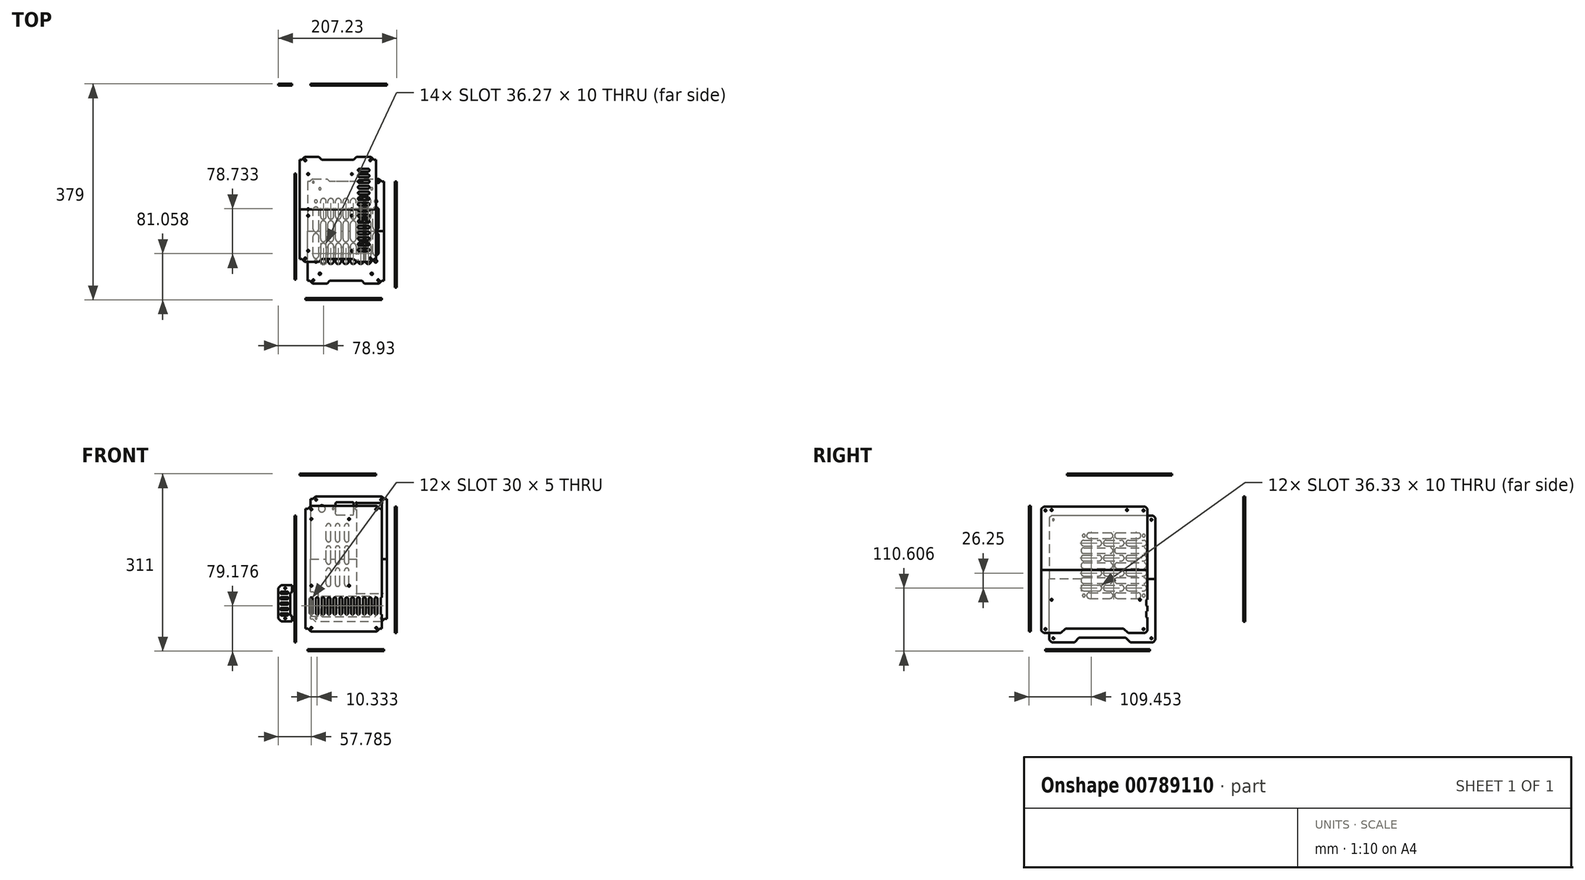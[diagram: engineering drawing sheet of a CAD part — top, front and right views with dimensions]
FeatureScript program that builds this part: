
annotation { "Feature Type Name" : "Feature", "Feature Type Description" : "" }
export const myFeature = defineFeature(function(context is Context, id is Id, definition is map)
    precondition{}
    {
        {
            var Q0;
            Q0=qCreatedBy(makeId("Front.planeOp"),FACE);
            var sketch = newSketch(context, id + "F0", { "sketchPlane" : qUnion([Q0])});
            skLineSegment(sketch, "E0.bottom", {"start": v(-76.44, 105.68) * mm, "end": v(57.56, 105.68) * mm});
            skLineSegment(sketch, "E0.top", {"start": v(-76.44, -8.32) * mm, "end": v(57.56, -8.32) * mm});
            skLineSegment(sketch, "E0.left", {"start": v(-76.44, 105.68) * mm, "end": v(-76.44, -8.32) * mm});
            skLineSegment(sketch, "E0.right", {"start": v(57.56, 105.68) * mm, "end": v(57.56, -8.32) * mm});
            skLineSegment(sketch, "E1", {"start": v(-76.44, 96.68) * mm, "end": v(-72.44, 96.68) * mm});
            skLineSegment(sketch, "E2", {"start": v(-72.44, 96.68) * mm, "end": v(-67.44, 101.68) * mm});
            skLineSegment(sketch, "E3", {"start": v(57.56, 96.68) * mm, "end": v(53.56, 96.68) * mm});
            skLineSegment(sketch, "E4", {"start": v(48.56, 101.68) * mm, "end": v(-67.44, 101.68) * mm});
            skLineSegment(sketch, "E5", {"start": v(48.56, 101.68) * mm, "end": v(53.56, 96.68) * mm});
            skLineSegment(sketch, "E6", {"start": v(-76.44, 95.68) * mm, "end": v(-66.44, 95.68) * mm, "construction": true});
            skCircle(sketch, "E7", {"center": v(-66.44, 95.68) * mm, "radius": 1.6 * mm});
            skLineSegment(sketch, "E8", {"start": v(57.56, 95.68) * mm, "end": v(47.56, 95.68) * mm, "construction": true});
            skCircle(sketch, "E9", {"center": v(47.56, 95.68) * mm, "radius": 1.6 * mm});
            skSolve(sketch);
        }
        {
            var Q0;
            {var subQ1=sQuery(id+"F0.wireOp",EDGE,"E0.top");Q0=makeQuery(id+"F0.imprint","IMPRINT",FACE,{"disambiguationData":[TD([[makeQuery(id+"F0.imprint","IMPRINT",EDGE,{"derivedFrom":subQ1}),1.0]])]});}
            extrude(context, id + "F1", {"entities" : qUnion([Q0]), "depth" : 3 * mm});
        }
        {
            var Q0;
            Q0=makeQuery(id+"F1.opExtrude","SWEPT_BODY",BODY,{"disambiguationData":[OSD([sQuery(id+"F0.wireOp",EDGE,"E0.bottom"),sQuery(id+"F0.wireOp",EDGE,"E0.top"),sQuery(id+"F0.wireOp",EDGE,"E0.left"),sQuery(id+"F0.wireOp",EDGE,"E0.right"),sQuery(id+"F0.wireOp",EDGE,"E1"),sQuery(id+"F0.wireOp",EDGE,"E2"),sQuery(id+"F0.wireOp",EDGE,"8kIEKiAh-QTEb-dtpp-JcTS-wpPMPQfBbqQd"),sQuery(id+"F0.wireOp",EDGE,"IAD0FTGy-GJaP-wMLm-guci-XfnhwucHu2uu"),sQuery(id+"F0.wireOp",EDGE,"IvHsRxJE-VIxi-RXbs-pRJC-tqeUj7lQNFDg"),sQuery(id+"F0.wireOp",EDGE,"jDx6nEBO-jJHg-Gf5S-wIms-nsZNRVFYcTxt")])]});
            var Q1;
            Q1=makeQuery(id+"F1.opExtrude","SWEPT_FACE",FACE,{"disambiguationData":[OSD([sQuery(id+"F0.wireOp",EDGE,"E0.top")])]});
            mirror(context, id + "F2", {"operationType" : NewBodyOperationType.ADD, "entities" : qUnion([Q0]), "mirrorPlane" : qUnion([Q1])});
        }
        {
            var Q0;
            {var subQ0=makeQuery(id+"F1.opExtrude","CAP_FACE",FACE,{"disambiguationData":[OSD([sQuery(id+"F0.wireOp",EDGE,"E0.bottom"),sQuery(id+"F0.wireOp",EDGE,"E0.top"),sQuery(id+"F0.wireOp",EDGE,"E0.left"),sQuery(id+"F0.wireOp",EDGE,"E0.right"),sQuery(id+"F0.wireOp",EDGE,"E1"),sQuery(id+"F0.wireOp",EDGE,"E2"),sQuery(id+"F0.wireOp",EDGE,"8kIEKiAh-QTEb-dtpp-JcTS-wpPMPQfBbqQd"),sQuery(id+"F0.wireOp",EDGE,"IAD0FTGy-GJaP-wMLm-guci-XfnhwucHu2uu"),sQuery(id+"F0.wireOp",EDGE,"IvHsRxJE-VIxi-RXbs-pRJC-tqeUj7lQNFDg"),sQuery(id+"F0.wireOp",EDGE,"jDx6nEBO-jJHg-Gf5S-wIms-nsZNRVFYcTxt")])],"isStart":false});Q0=makeQuery(id+"F2.boolean.opBoolean","MERGE",FACE,{"derivedFrom":[subQ0,makeQuery(id+"F2.opPattern","COPY",FACE,{"derivedFrom":subQ0,"instanceName":"1"})]});}
            var sketch = newSketch(context, id + "F3", { "sketchPlane" : qUnion([Q0])});
            skLineSegment(sketch, "E10", {"start": v(-66.44, -86.32) * mm, "end": v(-66.44, -118.32) * mm, "construction": true});
            skLineSegment(sketch, "E11.bottom", {"start": v(-66.44, 78.68) * mm, "end": v(-0.24, 78.68) * mm, "construction": true});
            skLineSegment(sketch, "E11.top", {"start": v(-66.44, -38.32) * mm, "end": v(-0.24, -38.32) * mm, "construction": true});
            skLineSegment(sketch, "E11.left", {"start": v(-66.44, 78.68) * mm, "end": v(-66.44, -38.32) * mm, "construction": true});
            skLineSegment(sketch, "E11.right", {"start": v(-0.24, 78.68) * mm, "end": v(-0.24, -38.32) * mm, "construction": true});
            skLineSegment(sketch, "E12", {"start": v(-66.44, 78.68) * mm, "end": v(-76.44, 78.68) * mm, "construction": true});
            skCircle(sketch, "E13", {"center": v(-0.24, 78.68) * mm, "radius": 1.6 * mm});
            skCircle(sketch, "E14", {"center": v(-66.44, 78.68) * mm, "radius": 1.6 * mm});
            skCircle(sketch, "E15", {"center": v(-66.44, -38.32) * mm, "radius": 1.6 * mm});
            skCircle(sketch, "E16", {"center": v(-0.24, -38.32) * mm, "radius": 1.6 * mm});
            skLineSegment(sketch, "E17", {"start": v(-66.44, -86.32) * mm, "end": v(-66.44, -61.32) * mm, "construction": true});
            skArc(sketch, "E18.0.startCap", {"start": v(-63.94, -86.32) * mm, "mid": v(-66.44, -88.82) * mm, "end": v(-68.94, -86.32) * mm});
            skArc(sketch, "E18.0.endCap", {"start": v(-68.94, -61.32) * mm, "mid": v(-66.44, -58.82) * mm, "end": v(-63.94, -61.32) * mm});
            skLineSegment(sketch, "E18.0.left", {"start": v(-68.94, -86.32) * mm, "end": v(-68.94, -61.32) * mm});
            skLineSegment(sketch, "E18.0.right", {"start": v(-63.94, -86.32) * mm, "end": v(-63.94, -61.32) * mm});
            skLineSegment(sketch, "E19.1.0.0", {"start": v(-56.11, -86.32) * mm, "end": v(-56.11, -61.32) * mm, "construction": true});
            skArc(sketch, "E19.1.0.1", {"start": v(-53.61, -86.32) * mm, "mid": v(-56.11, -88.82) * mm, "end": v(-58.61, -86.32) * mm});
            skArc(sketch, "E19.1.0.2", {"start": v(-58.61, -61.32) * mm, "mid": v(-56.11, -58.82) * mm, "end": v(-53.61, -61.32) * mm});
            skLineSegment(sketch, "E19.1.0.3", {"start": v(-53.61, -86.32) * mm, "end": v(-53.61, -61.32) * mm});
            skLineSegment(sketch, "E19.1.0.4", {"start": v(-58.61, -86.32) * mm, "end": v(-58.61, -61.32) * mm});
            skLineSegment(sketch, "E19.2.0.0", {"start": v(-45.78, -86.32) * mm, "end": v(-45.78, -61.32) * mm, "construction": true});
            skArc(sketch, "E19.2.0.1", {"start": v(-43.28, -86.32) * mm, "mid": v(-45.78, -88.82) * mm, "end": v(-48.28, -86.32) * mm});
            skArc(sketch, "E19.2.0.2", {"start": v(-48.28, -61.32) * mm, "mid": v(-45.78, -58.82) * mm, "end": v(-43.28, -61.32) * mm});
            skLineSegment(sketch, "E19.2.0.3", {"start": v(-43.28, -86.32) * mm, "end": v(-43.28, -61.32) * mm});
            skLineSegment(sketch, "E19.2.0.4", {"start": v(-48.28, -86.32) * mm, "end": v(-48.28, -61.32) * mm});
            skLineSegment(sketch, "E19.3.0.0", {"start": v(-35.45, -86.32) * mm, "end": v(-35.45, -61.32) * mm, "construction": true});
            skArc(sketch, "E19.3.0.1", {"start": v(-32.95, -86.32) * mm, "mid": v(-35.45, -88.82) * mm, "end": v(-37.95, -86.32) * mm});
            skArc(sketch, "E19.3.0.2", {"start": v(-37.95, -61.32) * mm, "mid": v(-35.45, -58.82) * mm, "end": v(-32.95, -61.32) * mm});
            skLineSegment(sketch, "E19.3.0.3", {"start": v(-32.95, -86.32) * mm, "end": v(-32.95, -61.32) * mm});
            skLineSegment(sketch, "E19.3.0.4", {"start": v(-37.95, -86.32) * mm, "end": v(-37.95, -61.32) * mm});
            skLineSegment(sketch, "E19.4.0.0", {"start": v(-25.11, -86.32) * mm, "end": v(-25.11, -61.32) * mm, "construction": true});
            skArc(sketch, "E19.4.0.1", {"start": v(-22.61, -86.32) * mm, "mid": v(-25.11, -88.82) * mm, "end": v(-27.61, -86.32) * mm});
            skArc(sketch, "E19.4.0.2", {"start": v(-27.61, -61.32) * mm, "mid": v(-25.11, -58.82) * mm, "end": v(-22.61, -61.32) * mm});
            skLineSegment(sketch, "E19.4.0.3", {"start": v(-22.61, -86.32) * mm, "end": v(-22.61, -61.32) * mm});
            skLineSegment(sketch, "E19.4.0.4", {"start": v(-27.61, -86.32) * mm, "end": v(-27.61, -61.32) * mm});
            skLineSegment(sketch, "E19.5.0.0", {"start": v(-14.78, -86.32) * mm, "end": v(-14.78, -61.32) * mm, "construction": true});
            skArc(sketch, "E19.5.0.1", {"start": v(-12.28, -86.32) * mm, "mid": v(-14.78, -88.82) * mm, "end": v(-17.28, -86.32) * mm});
            skArc(sketch, "E19.5.0.2", {"start": v(-17.28, -61.32) * mm, "mid": v(-14.78, -58.82) * mm, "end": v(-12.28, -61.32) * mm});
            skLineSegment(sketch, "E19.5.0.3", {"start": v(-12.28, -86.32) * mm, "end": v(-12.28, -61.32) * mm});
            skLineSegment(sketch, "E19.5.0.4", {"start": v(-17.28, -86.32) * mm, "end": v(-17.28, -61.32) * mm});
            skLineSegment(sketch, "E19.6.0.0", {"start": v(-4.45, -86.32) * mm, "end": v(-4.45, -61.32) * mm, "construction": true});
            skArc(sketch, "E19.6.0.1", {"start": v(-1.95, -86.32) * mm, "mid": v(-4.45, -88.82) * mm, "end": v(-6.95, -86.32) * mm});
            skArc(sketch, "E19.6.0.2", {"start": v(-6.95, -61.32) * mm, "mid": v(-4.45, -58.82) * mm, "end": v(-1.95, -61.32) * mm});
            skLineSegment(sketch, "E19.6.0.3", {"start": v(-1.95, -86.32) * mm, "end": v(-1.95, -61.32) * mm});
            skLineSegment(sketch, "E19.6.0.4", {"start": v(-6.95, -86.32) * mm, "end": v(-6.95, -61.32) * mm});
            skLineSegment(sketch, "E19.7.0.0", {"start": v(5.89, -86.32) * mm, "end": v(5.89, -61.32) * mm, "construction": true});
            skArc(sketch, "E19.7.0.1", {"start": v(8.39, -86.32) * mm, "mid": v(5.89, -88.82) * mm, "end": v(3.39, -86.32) * mm});
            skArc(sketch, "E19.7.0.2", {"start": v(3.39, -61.32) * mm, "mid": v(5.89, -58.82) * mm, "end": v(8.39, -61.32) * mm});
            skLineSegment(sketch, "E19.7.0.3", {"start": v(8.39, -86.32) * mm, "end": v(8.39, -61.32) * mm});
            skLineSegment(sketch, "E19.7.0.4", {"start": v(3.39, -86.32) * mm, "end": v(3.39, -61.32) * mm});
            skLineSegment(sketch, "E19.8.0.0", {"start": v(16.22, -86.32) * mm, "end": v(16.22, -61.32) * mm, "construction": true});
            skArc(sketch, "E19.8.0.1", {"start": v(18.72, -86.32) * mm, "mid": v(16.22, -88.82) * mm, "end": v(13.72, -86.32) * mm});
            skArc(sketch, "E19.8.0.2", {"start": v(13.72, -61.32) * mm, "mid": v(16.22, -58.82) * mm, "end": v(18.72, -61.32) * mm});
            skLineSegment(sketch, "E19.8.0.3", {"start": v(18.72, -86.32) * mm, "end": v(18.72, -61.32) * mm});
            skLineSegment(sketch, "E19.8.0.4", {"start": v(13.72, -86.32) * mm, "end": v(13.72, -61.32) * mm});
            skLineSegment(sketch, "E19.9.0.0", {"start": v(26.55, -86.32) * mm, "end": v(26.55, -61.32) * mm, "construction": true});
            skArc(sketch, "E19.9.0.1", {"start": v(29.05, -86.32) * mm, "mid": v(26.55, -88.82) * mm, "end": v(24.05, -86.32) * mm});
            skArc(sketch, "E19.9.0.2", {"start": v(24.05, -61.32) * mm, "mid": v(26.55, -58.82) * mm, "end": v(29.05, -61.32) * mm});
            skLineSegment(sketch, "E19.9.0.3", {"start": v(29.05, -86.32) * mm, "end": v(29.05, -61.32) * mm});
            skLineSegment(sketch, "E19.9.0.4", {"start": v(24.05, -86.32) * mm, "end": v(24.05, -61.32) * mm});
            skLineSegment(sketch, "E19.10.0.0", {"start": v(36.89, -86.32) * mm, "end": v(36.89, -61.32) * mm, "construction": true});
            skArc(sketch, "E19.10.0.1", {"start": v(39.39, -86.32) * mm, "mid": v(36.89, -88.82) * mm, "end": v(34.39, -86.32) * mm});
            skArc(sketch, "E19.10.0.2", {"start": v(34.39, -61.32) * mm, "mid": v(36.89, -58.82) * mm, "end": v(39.39, -61.32) * mm});
            skLineSegment(sketch, "E19.10.0.3", {"start": v(39.39, -86.32) * mm, "end": v(39.39, -61.32) * mm});
            skLineSegment(sketch, "E19.10.0.4", {"start": v(34.39, -86.32) * mm, "end": v(34.39, -61.32) * mm});
            skLineSegment(sketch, "E19.11.0.0", {"start": v(47.22, -86.32) * mm, "end": v(47.22, -61.32) * mm, "construction": true});
            skArc(sketch, "E19.11.0.1", {"start": v(49.72, -86.32) * mm, "mid": v(47.22, -88.82) * mm, "end": v(44.72, -86.32) * mm});
            skArc(sketch, "E19.11.0.2", {"start": v(44.72, -61.32) * mm, "mid": v(47.22, -58.82) * mm, "end": v(49.72, -61.32) * mm});
            skLineSegment(sketch, "E19.11.0.3", {"start": v(49.72, -86.32) * mm, "end": v(49.72, -61.32) * mm});
            skLineSegment(sketch, "E19.11.0.4", {"start": v(44.72, -86.32) * mm, "end": v(44.72, -61.32) * mm});
            skLineSegment(sketch, "E19.12.0.0", {"start": v(57.55, -86.32) * mm, "end": v(57.55, -61.32) * mm, "construction": true});
            skArc(sketch, "E19.12.0.1", {"start": v(60.05, -86.32) * mm, "mid": v(57.55, -88.82) * mm, "end": v(55.05, -86.32) * mm});
            skArc(sketch, "E19.12.0.2", {"start": v(55.05, -61.32) * mm, "mid": v(57.55, -58.82) * mm, "end": v(60.05, -61.32) * mm});
            skLineSegment(sketch, "E19.12.0.3", {"start": v(60.05, -86.32) * mm, "end": v(60.05, -61.32) * mm});
            skLineSegment(sketch, "E19.12.0.4", {"start": v(55.05, -86.32) * mm, "end": v(55.05, -61.32) * mm});
            skLineSegment(sketch, "E19.direction1", {"start": v(-68.94, -86.32) * mm, "end": v(-58.61, -86.32) * mm, "construction": true});
            skSolve(sketch);
        }
        {
            var Q0;
            Q0=qSketchRegion(id+"F3",true);
            extrude(context, id + "F4", {"entities" : qUnion([Q0]), "operationType" : NewBodyOperationType.REMOVE, "oppositeDirection" : true, "depth" : 3 * mm});
        }
        {
            var Q0;
            Q0=qCreatedBy(makeId("Right.planeOp"),FACE);
            cPlane(context, id + "F5", {"entities" : qUnion([Q0]), "cplaneType" : CPlaneType.OFFSET, "offset" : 80 * mm, "width" : 150 * mm, "height" : 150 * mm});
        }
        {
            var Q0;
            Q0=qCreatedBy(id+"F5.planeOp",FACE);
            var sketch = newSketch(context, id + "F6", { "sketchPlane" : qUnion([Q0])});
            skLineSegment(sketch, "E20.bottom", {"start": v(18.91, 100.63) * mm, "end": v(204.91, 100.63) * mm});
            skLineSegment(sketch, "E20.top", {"start": v(18.91, -10.37) * mm, "end": v(204.91, -10.37) * mm});
            skLineSegment(sketch, "E20.left", {"start": v(18.91, 100.63) * mm, "end": v(18.91, -10.37) * mm});
            skLineSegment(sketch, "E20.right", {"start": v(204.91, 100.63) * mm, "end": v(204.91, -10.37) * mm});
            skLineSegment(sketch, "E21", {"start": v(18.91, 96.63) * mm, "end": v(22.91, 100.63) * mm});
            skLineSegment(sketch, "E22", {"start": v(200.91, 100.63) * mm, "end": v(204.91, 96.63) * mm});
            skLineSegment(sketch, "E23", {"start": v(18.91, 93.63) * mm, "end": v(25.91, 93.63) * mm, "construction": true});
            skCircle(sketch, "E24", {"center": v(25.91, 93.63) * mm, "radius": 1.6 * mm});
            skLineSegment(sketch, "E25", {"start": v(204.91, 93.63) * mm, "end": v(197.91, 93.63) * mm, "construction": true});
            skCircle(sketch, "E26", {"center": v(197.91, 93.63) * mm, "radius": 1.6 * mm});
            skSolve(sketch);
        }
        {
            var Q0;
            {var subQ4=sQuery(id+"F6.wireOp",EDGE,"E20.top");Q0=makeQuery(id+"F6.imprint","IMPRINT",FACE,{"disambiguationData":[TD([[makeQuery(id+"F6.imprint","IMPRINT",EDGE,{"derivedFrom":subQ4}),1.0]])]});}
            extrude(context, id + "F7", {"entities" : qUnion([Q0]), "depth" : 3 * mm});
        }
        {
            var Q0;
            Q0=makeQuery(id+"F7.opExtrude","SWEPT_BODY",BODY,{"disambiguationData":[OSD([sQuery(id+"F6.wireOp",EDGE,"E20.bottom"),sQuery(id+"F6.wireOp",EDGE,"E20.top"),sQuery(id+"F6.wireOp",EDGE,"E20.left"),sQuery(id+"F6.wireOp",EDGE,"E20.right"),sQuery(id+"F6.wireOp",EDGE,"uhohLnhp-hqEh-HnCf-sw5P-UAyFwgDYjcBT"),sQuery(id+"F6.wireOp",EDGE,"PZ9vbapj-Vyhe-IVd5-wSIB-ihSb0FTefDFo"),sQuery(id+"F6.wireOp",EDGE,"Vy2RlQAS-aQ6k-OJzX-lqoE-WAFZ4NoHzz8E"),sQuery(id+"F6.wireOp",EDGE,"uOpGianr-bHoC-LPpd-ZrnQ-WT6fRq75YZDk"),sQuery(id+"F6.wireOp",EDGE,"ByD4MoDk-9vtG-w2Bj-nV2I-deXss6nWGu8L"),sQuery(id+"F6.wireOp",EDGE,"dErzSW6J-HGX5-GNXE-lozc-OmhnMsFbACEc"),sQuery(id+"F6.wireOp",EDGE,"oiYVu7ST-duG0-g5FE-uATR-zlAqLM0uh895"),sQuery(id+"F6.wireOp",EDGE,"fhnCciFL-T4Vn-rBCZ-nkKt-uSig2OXv9zq8")])]});
            var Q1;
            Q1=makeQuery(id+"F7.opExtrude","SWEPT_FACE",FACE,{"disambiguationData":[OSD([sQuery(id+"F6.wireOp",EDGE,"E20.top")])]});
            mirror(context, id + "F8", {"operationType" : NewBodyOperationType.ADD, "entities" : qUnion([Q0]), "mirrorPlane" : qUnion([Q1])});
        }
        {
            var Q0;
            {var subQ0=makeQuery(id+"F7.opExtrude","CAP_FACE",FACE,{"disambiguationData":[OSD([sQuery(id+"F6.wireOp",EDGE,"E20.bottom"),sQuery(id+"F6.wireOp",EDGE,"E20.top"),sQuery(id+"F6.wireOp",EDGE,"E20.left"),sQuery(id+"F6.wireOp",EDGE,"E20.right"),sQuery(id+"F6.wireOp",EDGE,"E21"),sQuery(id+"F6.wireOp",EDGE,"E22")])],"isStart":true});Q0=makeQuery(id+"F8.boolean.opBoolean","MERGE",FACE,{"derivedFrom":[subQ0,makeQuery(id+"F8.opPattern","COPY",FACE,{"derivedFrom":subQ0,"instanceName":"1"})]});}
            var sketch = newSketch(context, id + "F9", { "sketchPlane" : qUnion([Q0])});
            skLineSegment(sketch, "E27", {"start": v(-201.91, -69.37) * mm, "end": v(-201.91, 100.63) * mm, "construction": true});
            skLineSegment(sketch, "E28", {"start": v(-201.91, -69.37) * mm, "end": v(-31.91, -69.37) * mm, "construction": true});
            skLineSegment(sketch, "E29", {"start": v(-201.91, 100.63) * mm, "end": v(-31.91, 100.63) * mm, "construction": true});
            skLineSegment(sketch, "E30", {"start": v(-31.91, 100.63) * mm, "end": v(-31.91, -69.37) * mm, "construction": true});
            skLineSegment(sketch, "E31", {"start": v(-201.91, -62.97) * mm, "end": v(-191.71, -62.97) * mm, "construction": true});
            skCircle(sketch, "E32", {"center": v(-191.71, -62.97) * mm, "radius": 1.5 * mm});
            skLineSegment(sketch, "E33", {"start": v(-191.71, -62.97) * mm, "end": v(-36.81, -62.97) * mm, "construction": true});
            skCircle(sketch, "E34", {"center": v(-36.81, -62.97) * mm, "radius": 1.5 * mm});
            skLineSegment(sketch, "E35", {"start": v(-201.91, 94.43) * mm, "end": v(-168.91, 94.43) * mm, "construction": true});
            skCircle(sketch, "E36", {"center": v(-168.91, 94.43) * mm, "radius": 1.5 * mm});
            skLineSegment(sketch, "E37", {"start": v(-168.91, 94.43) * mm, "end": v(-36.81, 94.43) * mm, "construction": true});
            skCircle(sketch, "E38", {"center": v(-36.81, 94.43) * mm, "radius": 1.5 * mm});
            skLineSegment(sketch, "E39", {"start": v(-52.91, -121.37) * mm, "end": v(-60.91, -113.37) * mm});
            skLineSegment(sketch, "E40", {"start": v(-60.91, -113.37) * mm, "end": v(-162.91, -113.37) * mm});
            skLineSegment(sketch, "E41", {"start": v(-162.91, -113.37) * mm, "end": v(-170.91, -121.37) * mm});
            skLineSegment(sketch, "E42", {"start": v(-52.91, -121.37) * mm, "end": v(-170.91, -121.37) * mm});
            skLineSegment(sketch, "E43.bottom", {"start": v(-202.91, -62.57) * mm, "end": v(-204.91, -62.57) * mm});
            skLineSegment(sketch, "E43.top", {"start": v(-202.91, -73.57) * mm, "end": v(-204.91, -73.57) * mm});
            skLineSegment(sketch, "E43.left", {"start": v(-202.91, -62.57) * mm, "end": v(-202.91, -73.57) * mm});
            skLineSegment(sketch, "E43.right", {"start": v(-204.91, -62.57) * mm, "end": v(-204.91, -73.57) * mm});
            skLineSegment(sketch, "E44", {"start": v(-202.91, -68.07) * mm, "end": v(-201.91, -68.07) * mm, "construction": true});
            skLineSegment(sketch, "E45.bottom", {"start": v(-202.91, -82.87) * mm, "end": v(-204.91, -82.87) * mm});
            skLineSegment(sketch, "E45.top", {"start": v(-202.91, -93.87) * mm, "end": v(-204.91, -93.87) * mm});
            skLineSegment(sketch, "E45.left", {"start": v(-202.91, -82.87) * mm, "end": v(-202.91, -93.87) * mm});
            skLineSegment(sketch, "E45.right", {"start": v(-204.91, -82.87) * mm, "end": v(-204.91, -93.87) * mm});
            skLineSegment(sketch, "E46", {"start": v(-204.91, -82.87) * mm, "end": v(-204.91, -73.57) * mm, "construction": true});
            skLineSegment(sketch, "E47", {"start": v(-202.91, -73.57) * mm, "end": v(-202.91, -82.87) * mm, "construction": true});
            skLineSegment(sketch, "E48", {"start": v(-204.91, -88.37) * mm, "end": v(-207.88, -88.37) * mm, "construction": true});
            skLineSegment(sketch, "E49", {"start": v(-207.88, -88.37) * mm, "end": v(-207.88, -68.07) * mm, "construction": true});
            skPoint(sketch, "E49.endSnap0", {"position": v(-204.91, -68.07) * mm});
            skLineSegment(sketch, "E50", {"start": v(-207.88, -68.07) * mm, "end": v(-204.91, -68.07) * mm, "construction": true});
            skSolve(sketch);
        }
        {
            var Q0;
            Q0=qSketchRegion(id+"F9",true);
            var Q1;
            {var subQ0=sQuery(id+"F9.wireOp",EDGE,"b6TVsvgF-kPWZ-6Ni7-LZi2-MRGtpnM4VBQ9");Q1=makeQuery(id+"F9.imprint","IMPRINT",FACE,{"disambiguationData":[TD([[makeQuery(id+"F9.imprint","IMPRINT",EDGE,{"derivedFrom":subQ0}),-1.0]])]});}
            extrude(context, id + "F10", {"entities" : qUnion([Q0, Q1]), "operationType" : NewBodyOperationType.REMOVE, "oppositeDirection" : true, "depth" : 25 * mm});
        }
        {
            var Q0;
            Q0=qCreatedBy(makeId("Right.planeOp"),FACE);
            cPlane(context, id + "F11", {"entities" : qUnion([Q0]), "cplaneType" : CPlaneType.OFFSET, "offset" : 96 * mm, "oppositeDirection" : true, "width" : 150 * mm, "height" : 150 * mm});
        }
        {
            var Q0;
            Q0=qCreatedBy(id+"F11.planeOp",FACE);
            var sketch = newSketch(context, id + "F12", { "sketchPlane" : qUnion([Q0])});
            skLineSegment(sketch, "E51.bottom", {"start": v(218.79, 84.48) * mm, "end": v(32.79, 84.48) * mm});
            skLineSegment(sketch, "E51.top", {"start": v(218.79, -26.52) * mm, "end": v(32.79, -26.52) * mm});
            skLineSegment(sketch, "E51.left", {"start": v(218.79, 84.48) * mm, "end": v(218.79, -26.52) * mm});
            skLineSegment(sketch, "E51.right", {"start": v(32.79, 84.48) * mm, "end": v(32.79, -26.52) * mm});
            skLineSegment(sketch, "E52", {"start": v(218.79, 80.48) * mm, "end": v(214.79, 84.48) * mm});
            skLineSegment(sketch, "E53", {"start": v(36.79, 84.48) * mm, "end": v(32.79, 80.48) * mm});
            skLineSegment(sketch, "E54", {"start": v(218.79, 77.48) * mm, "end": v(211.79, 77.48) * mm, "construction": true});
            skCircle(sketch, "E55", {"center": v(211.79, 77.48) * mm, "radius": 1.6 * mm});
            skLineSegment(sketch, "E56", {"start": v(32.79, 77.48) * mm, "end": v(39.79, 77.48) * mm, "construction": true});
            skCircle(sketch, "E57", {"center": v(39.79, 77.48) * mm, "radius": 1.6 * mm});
            skSolve(sketch);
        }
        {
            var Q0;
            {var subQ1=sQuery(id+"F12.wireOp",EDGE,"E51.top");Q0=makeQuery(id+"F12.imprint","IMPRINT",FACE,{"disambiguationData":[TD([[makeQuery(id+"F12.imprint","IMPRINT",EDGE,{"derivedFrom":subQ1}),-1.0]])]});}
            extrude(context, id + "F13", {"entities" : qUnion([Q0]), "depth" : 3 * mm});
        }
        {
            var Q0;
            Q0=makeQuery(id+"F13.opExtrude","SWEPT_BODY",BODY,{"disambiguationData":[OSD([sQuery(id+"F12.wireOp",EDGE,"E51.bottom"),sQuery(id+"F12.wireOp",EDGE,"E51.top"),sQuery(id+"F12.wireOp",EDGE,"E51.left"),sQuery(id+"F12.wireOp",EDGE,"E51.right"),sQuery(id+"F12.wireOp",EDGE,"E52"),sQuery(id+"F12.wireOp",EDGE,"E53")])]});
            var Q1;
            Q1=makeQuery(id+"F13.opExtrude","SWEPT_FACE",FACE,{"disambiguationData":[OSD([sQuery(id+"F12.wireOp",EDGE,"E51.top")])]});
            mirror(context, id + "F14", {"operationType" : NewBodyOperationType.ADD, "entities" : qUnion([Q0]), "mirrorPlane" : qUnion([Q1])});
        }
        {
            var Q0;
            {var subQ0=makeQuery(id+"F13.opExtrude","CAP_FACE",FACE,{"disambiguationData":[OSD([sQuery(id+"F12.wireOp",EDGE,"E51.bottom"),sQuery(id+"F12.wireOp",EDGE,"E51.top"),sQuery(id+"F12.wireOp",EDGE,"E51.left"),sQuery(id+"F12.wireOp",EDGE,"E51.right"),sQuery(id+"F12.wireOp",EDGE,"E52"),sQuery(id+"F12.wireOp",EDGE,"E53")])],"isStart":true});Q0=makeQuery(id+"F14.boolean.opBoolean","MERGE",FACE,{"derivedFrom":[subQ0,makeQuery(id+"F14.opPattern","COPY",FACE,{"derivedFrom":subQ0,"instanceName":"1"})]});}
            var sketch = newSketch(context, id + "F15", { "sketchPlane" : qUnion([Q0])});
            skLineSegment(sketch, "E58", {"start": v(-218.79, 54.48) * mm, "end": v(-198.29, 54.48) * mm, "construction": true});
            skLineSegment(sketch, "E59", {"start": v(-198.29, 54.48) * mm, "end": v(-198.29, -60.52) * mm, "construction": true});
            skLineSegment(sketch, "E60", {"start": v(-198.29, 49.48) * mm, "end": v(-188.29, 49.48) * mm, "construction": true});
            skLineSegment(sketch, "E61", {"start": v(-188.29, 49.48) * mm, "end": v(-152.29, 49.48) * mm, "construction": true});
            skLineSegment(sketch, "E62", {"start": v(-198.29, 36.36) * mm, "end": v(-171.95, 36.36) * mm, "construction": true});
            skLineSegment(sketch, "E63", {"start": v(-198.29, 23.23) * mm, "end": v(-152.29, 23.23) * mm, "construction": true});
            skLineSegment(sketch, "E64", {"start": v(-198.29, 10.1) * mm, "end": v(-171.95, 10.1) * mm, "construction": true});
            skLineSegment(sketch, "E65", {"start": v(-198.29, -3.02) * mm, "end": v(-152.29, -3.02) * mm, "construction": true});
            skLineSegment(sketch, "E66", {"start": v(-198.29, -16.14) * mm, "end": v(-171.95, -16.14) * mm, "construction": true});
            skLineSegment(sketch, "E67", {"start": v(-198.29, -29.27) * mm, "end": v(-152.29, -29.27) * mm, "construction": true});
            skLineSegment(sketch, "E68", {"start": v(-198.29, -42.4) * mm, "end": v(-171.95, -42.4) * mm, "construction": true});
            skLineSegment(sketch, "E69", {"start": v(-198.29, -55.52) * mm, "end": v(-188.29, -55.52) * mm, "construction": true});
            skLineSegment(sketch, "E70", {"start": v(-188.29, -55.52) * mm, "end": v(-152.29, -55.52) * mm, "construction": true});
            skCircle(sketch, "E71", {"center": v(-198.29, 49.48) * mm, "radius": 2.55 * mm});
            skLineSegment(sketch, "E72", {"start": v(-103.29, 49.48) * mm, "end": v(-93.29, 49.48) * mm, "construction": true});
            skPoint(sketch, "E72.endSnap0", {"position": v(-82.69, 49.48) * mm});
            skCircle(sketch, "E73", {"center": v(-93.29, 49.48) * mm, "radius": 2.55 * mm});
            skLineSegment(sketch, "E74", {"start": v(-152.29, 49.48) * mm, "end": v(-139.29, 49.48) * mm, "construction": true});
            skLineSegment(sketch, "E75", {"start": v(-139.29, 49.48) * mm, "end": v(-103.29, 49.48) * mm, "construction": true});
            skArc(sketch, "E76.0.startCap", {"start": v(-188.29, 44.48) * mm, "mid": v(-193.29, 49.48) * mm, "end": v(-188.29, 54.48) * mm});
            skArc(sketch, "E76.0.endCap", {"start": v(-152.29, 54.48) * mm, "mid": v(-147.29, 49.48) * mm, "end": v(-152.29, 44.48) * mm});
            skLineSegment(sketch, "E76.0.left", {"start": v(-188.29, 54.48) * mm, "end": v(-152.29, 54.48) * mm});
            skLineSegment(sketch, "E76.0.right", {"start": v(-188.29, 44.48) * mm, "end": v(-152.29, 44.48) * mm});
            skArc(sketch, "E76.1.startCap", {"start": v(-139.29, 44.48) * mm, "mid": v(-144.29, 49.48) * mm, "end": v(-139.29, 54.48) * mm});
            skArc(sketch, "E76.1.endCap", {"start": v(-103.29, 54.48) * mm, "mid": v(-98.29, 49.48) * mm, "end": v(-103.29, 44.48) * mm});
            skLineSegment(sketch, "E76.1.left", {"start": v(-139.29, 54.48) * mm, "end": v(-103.29, 54.48) * mm});
            skLineSegment(sketch, "E76.1.right", {"start": v(-139.29, 44.48) * mm, "end": v(-103.29, 44.48) * mm});
            skLineSegment(sketch, "E77", {"start": v(-171.95, 36.36) * mm, "end": v(-158.95, 36.36) * mm, "construction": true});
            skLineSegment(sketch, "E78", {"start": v(-158.95, 36.36) * mm, "end": v(-132.62, 36.36) * mm, "construction": true});
            skLineSegment(sketch, "E79", {"start": v(-132.62, 36.36) * mm, "end": v(-119.62, 36.36) * mm, "construction": true});
            skLineSegment(sketch, "E80", {"start": v(-119.62, 36.36) * mm, "end": v(-93.29, 36.36) * mm, "construction": true});
            skArc(sketch, "E81.0.startCap", {"start": v(-198.29, 31.36) * mm, "mid": v(-203.29, 36.36) * mm, "end": v(-198.29, 41.36) * mm});
            skArc(sketch, "E81.0.endCap", {"start": v(-171.95, 41.36) * mm, "mid": v(-166.95, 36.36) * mm, "end": v(-171.95, 31.36) * mm});
            skLineSegment(sketch, "E81.0.left", {"start": v(-198.29, 41.36) * mm, "end": v(-171.95, 41.36) * mm});
            skLineSegment(sketch, "E81.0.right", {"start": v(-198.29, 31.36) * mm, "end": v(-171.95, 31.36) * mm});
            skArc(sketch, "E81.1.startCap", {"start": v(-158.95, 31.36) * mm, "mid": v(-163.95, 36.36) * mm, "end": v(-158.95, 41.36) * mm});
            skArc(sketch, "E81.1.endCap", {"start": v(-132.62, 41.36) * mm, "mid": v(-127.62, 36.36) * mm, "end": v(-132.62, 31.36) * mm});
            skLineSegment(sketch, "E81.1.left", {"start": v(-158.95, 41.36) * mm, "end": v(-132.62, 41.36) * mm});
            skLineSegment(sketch, "E81.1.right", {"start": v(-158.95, 31.36) * mm, "end": v(-132.62, 31.36) * mm});
            skArc(sketch, "E81.2.startCap", {"start": v(-119.62, 31.36) * mm, "mid": v(-124.62, 36.36) * mm, "end": v(-119.62, 41.36) * mm});
            skArc(sketch, "E81.2.endCap", {"start": v(-93.29, 41.36) * mm, "mid": v(-88.29, 36.36) * mm, "end": v(-93.29, 31.36) * mm});
            skLineSegment(sketch, "E81.2.left", {"start": v(-119.62, 41.36) * mm, "end": v(-93.29, 41.36) * mm});
            skLineSegment(sketch, "E81.2.right", {"start": v(-119.62, 31.36) * mm, "end": v(-93.29, 31.36) * mm});
            skLineSegment(sketch, "E82", {"start": v(-152.29, 23.23) * mm, "end": v(-139.29, 23.23) * mm, "construction": true});
            skLineSegment(sketch, "E83", {"start": v(-139.29, 23.23) * mm, "end": v(-93.29, 23.23) * mm, "construction": true});
            skArc(sketch, "E84.0.startCap", {"start": v(-198.29, 18.23) * mm, "mid": v(-203.29, 23.23) * mm, "end": v(-198.29, 28.23) * mm});
            skArc(sketch, "E84.0.endCap", {"start": v(-152.29, 28.23) * mm, "mid": v(-147.29, 23.23) * mm, "end": v(-152.29, 18.23) * mm});
            skLineSegment(sketch, "E84.0.left", {"start": v(-198.29, 28.23) * mm, "end": v(-152.29, 28.23) * mm});
            skLineSegment(sketch, "E84.0.right", {"start": v(-198.29, 18.23) * mm, "end": v(-152.29, 18.23) * mm});
            skArc(sketch, "E84.1.startCap", {"start": v(-139.29, 18.23) * mm, "mid": v(-144.29, 23.23) * mm, "end": v(-139.29, 28.23) * mm});
            skArc(sketch, "E84.1.endCap", {"start": v(-93.29, 28.23) * mm, "mid": v(-88.29, 23.23) * mm, "end": v(-93.29, 18.23) * mm});
            skLineSegment(sketch, "E84.1.left", {"start": v(-139.29, 28.23) * mm, "end": v(-93.29, 28.23) * mm});
            skLineSegment(sketch, "E84.1.right", {"start": v(-139.29, 18.23) * mm, "end": v(-93.29, 18.23) * mm});
            skLineSegment(sketch, "E85", {"start": v(-171.95, 10.1) * mm, "end": v(-158.95, 10.1) * mm, "construction": true});
            skLineSegment(sketch, "E86", {"start": v(-158.95, 10.1) * mm, "end": v(-132.62, 10.1) * mm, "construction": true});
            skLineSegment(sketch, "E87", {"start": v(-132.62, 10.1) * mm, "end": v(-119.62, 10.1) * mm, "construction": true});
            skLineSegment(sketch, "E88", {"start": v(-119.62, 10.1) * mm, "end": v(-93.29, 10.1) * mm, "construction": true});
            skArc(sketch, "E89.0.startCap", {"start": v(-198.29, 5.1) * mm, "mid": v(-203.29, 10.1) * mm, "end": v(-198.29, 15.1) * mm});
            skArc(sketch, "E89.0.endCap", {"start": v(-171.95, 15.1) * mm, "mid": v(-166.95, 10.1) * mm, "end": v(-171.95, 5.1) * mm});
            skLineSegment(sketch, "E89.0.left", {"start": v(-198.29, 15.1) * mm, "end": v(-171.95, 15.1) * mm});
            skLineSegment(sketch, "E89.0.right", {"start": v(-198.29, 5.1) * mm, "end": v(-171.95, 5.1) * mm});
            skArc(sketch, "E89.1.startCap", {"start": v(-158.95, 5.1) * mm, "mid": v(-163.95, 10.1) * mm, "end": v(-158.95, 15.1) * mm});
            skArc(sketch, "E89.1.endCap", {"start": v(-132.62, 15.1) * mm, "mid": v(-127.62, 10.1) * mm, "end": v(-132.62, 5.1) * mm});
            skLineSegment(sketch, "E89.1.left", {"start": v(-158.95, 15.1) * mm, "end": v(-132.62, 15.1) * mm});
            skLineSegment(sketch, "E89.1.right", {"start": v(-158.95, 5.1) * mm, "end": v(-132.62, 5.1) * mm});
            skArc(sketch, "E89.2.startCap", {"start": v(-119.62, 5.1) * mm, "mid": v(-124.62, 10.1) * mm, "end": v(-119.62, 15.1) * mm});
            skArc(sketch, "E89.2.endCap", {"start": v(-93.29, 15.1) * mm, "mid": v(-88.29, 10.1) * mm, "end": v(-93.29, 5.1) * mm});
            skLineSegment(sketch, "E89.2.left", {"start": v(-119.62, 15.1) * mm, "end": v(-93.29, 15.1) * mm});
            skLineSegment(sketch, "E89.2.right", {"start": v(-119.62, 5.1) * mm, "end": v(-93.29, 5.1) * mm});
            skLineSegment(sketch, "E90", {"start": v(-152.29, -3.02) * mm, "end": v(-139.29, -3.02) * mm, "construction": true});
            skLineSegment(sketch, "E91", {"start": v(-139.29, -3.02) * mm, "end": v(-93.29, -3.02) * mm, "construction": true});
            skLineSegment(sketch, "E92", {"start": v(-171.95, -16.14) * mm, "end": v(-158.95, -16.14) * mm, "construction": true});
            skLineSegment(sketch, "E93", {"start": v(-158.95, -16.14) * mm, "end": v(-132.62, -16.14) * mm, "construction": true});
            skLineSegment(sketch, "E94", {"start": v(-132.62, -16.14) * mm, "end": v(-119.62, -16.14) * mm, "construction": true});
            skLineSegment(sketch, "E95", {"start": v(-119.62, -16.14) * mm, "end": v(-93.29, -16.14) * mm, "construction": true});
            skLineSegment(sketch, "E96", {"start": v(-152.29, -29.27) * mm, "end": v(-139.29, -29.27) * mm, "construction": true});
            skLineSegment(sketch, "E97", {"start": v(-139.29, -29.27) * mm, "end": v(-93.29, -29.27) * mm, "construction": true});
            skLineSegment(sketch, "E98", {"start": v(-171.95, -42.4) * mm, "end": v(-158.95, -42.4) * mm, "construction": true});
            skLineSegment(sketch, "E99", {"start": v(-158.95, -42.4) * mm, "end": v(-132.62, -42.4) * mm, "construction": true});
            skLineSegment(sketch, "E100", {"start": v(-132.62, -42.4) * mm, "end": v(-119.62, -42.4) * mm, "construction": true});
            skLineSegment(sketch, "E101", {"start": v(-119.62, -42.4) * mm, "end": v(-93.29, -42.4) * mm, "construction": true});
            skLineSegment(sketch, "E102", {"start": v(-152.29, -55.52) * mm, "end": v(-139.29, -55.52) * mm, "construction": true});
            skLineSegment(sketch, "E103", {"start": v(-139.29, -55.52) * mm, "end": v(-103.29, -55.52) * mm, "construction": true});
            skLineSegment(sketch, "E104", {"start": v(-103.29, -55.52) * mm, "end": v(-93.29, -55.52) * mm, "construction": true});
            skArc(sketch, "E105.0.startCap", {"start": v(-198.29, -8.02) * mm, "mid": v(-203.29, -3.02) * mm, "end": v(-198.29, 1.98) * mm});
            skArc(sketch, "E105.0.endCap", {"start": v(-152.29, 1.98) * mm, "mid": v(-147.29, -3.02) * mm, "end": v(-152.29, -8.02) * mm});
            skLineSegment(sketch, "E105.0.left", {"start": v(-198.29, 1.98) * mm, "end": v(-152.29, 1.98) * mm});
            skLineSegment(sketch, "E105.0.right", {"start": v(-198.29, -8.02) * mm, "end": v(-152.29, -8.02) * mm});
            skArc(sketch, "E105.1.startCap", {"start": v(-139.29, -8.02) * mm, "mid": v(-144.29, -3.02) * mm, "end": v(-139.29, 1.98) * mm});
            skArc(sketch, "E105.1.endCap", {"start": v(-93.29, 1.98) * mm, "mid": v(-88.29, -3.02) * mm, "end": v(-93.29, -8.02) * mm});
            skLineSegment(sketch, "E105.1.left", {"start": v(-139.29, 1.98) * mm, "end": v(-93.29, 1.98) * mm});
            skLineSegment(sketch, "E105.1.right", {"start": v(-139.29, -8.02) * mm, "end": v(-93.29, -8.02) * mm});
            skArc(sketch, "E105.2.startCap", {"start": v(-198.29, -21.14) * mm, "mid": v(-203.29, -16.14) * mm, "end": v(-198.29, -11.14) * mm});
            skArc(sketch, "E105.2.endCap", {"start": v(-171.95, -11.14) * mm, "mid": v(-166.95, -16.14) * mm, "end": v(-171.95, -21.14) * mm});
            skLineSegment(sketch, "E105.2.left", {"start": v(-198.29, -11.14) * mm, "end": v(-171.95, -11.14) * mm});
            skLineSegment(sketch, "E105.2.right", {"start": v(-198.29, -21.14) * mm, "end": v(-171.95, -21.14) * mm});
            skArc(sketch, "E105.3.startCap", {"start": v(-158.95, -21.14) * mm, "mid": v(-163.95, -16.14) * mm, "end": v(-158.95, -11.14) * mm});
            skArc(sketch, "E105.3.endCap", {"start": v(-132.62, -11.14) * mm, "mid": v(-127.62, -16.14) * mm, "end": v(-132.62, -21.14) * mm});
            skLineSegment(sketch, "E105.3.left", {"start": v(-158.95, -11.14) * mm, "end": v(-132.62, -11.14) * mm});
            skLineSegment(sketch, "E105.3.right", {"start": v(-158.95, -21.14) * mm, "end": v(-132.62, -21.14) * mm});
            skArc(sketch, "E105.4.startCap", {"start": v(-119.62, -21.14) * mm, "mid": v(-124.62, -16.14) * mm, "end": v(-119.62, -11.14) * mm});
            skArc(sketch, "E105.4.endCap", {"start": v(-93.29, -11.14) * mm, "mid": v(-88.29, -16.14) * mm, "end": v(-93.29, -21.14) * mm});
            skLineSegment(sketch, "E105.4.left", {"start": v(-119.62, -11.14) * mm, "end": v(-93.29, -11.14) * mm});
            skLineSegment(sketch, "E105.4.right", {"start": v(-119.62, -21.14) * mm, "end": v(-93.29, -21.14) * mm});
            skArc(sketch, "E106.0.startCap", {"start": v(-198.29, -34.27) * mm, "mid": v(-203.29, -29.27) * mm, "end": v(-198.29, -24.27) * mm});
            skArc(sketch, "E106.0.endCap", {"start": v(-152.29, -24.27) * mm, "mid": v(-147.29, -29.27) * mm, "end": v(-152.29, -34.27) * mm});
            skLineSegment(sketch, "E106.0.left", {"start": v(-198.29, -24.27) * mm, "end": v(-152.29, -24.27) * mm});
            skLineSegment(sketch, "E106.0.right", {"start": v(-198.29, -34.27) * mm, "end": v(-152.29, -34.27) * mm});
            skArc(sketch, "E106.1.startCap", {"start": v(-139.29, -34.27) * mm, "mid": v(-144.29, -29.27) * mm, "end": v(-139.29, -24.27) * mm});
            skArc(sketch, "E106.1.endCap", {"start": v(-93.29, -24.27) * mm, "mid": v(-88.29, -29.27) * mm, "end": v(-93.29, -34.27) * mm});
            skLineSegment(sketch, "E106.1.left", {"start": v(-139.29, -24.27) * mm, "end": v(-93.29, -24.27) * mm});
            skLineSegment(sketch, "E106.1.right", {"start": v(-139.29, -34.27) * mm, "end": v(-93.29, -34.27) * mm});
            skArc(sketch, "E106.2.startCap", {"start": v(-198.29, -47.4) * mm, "mid": v(-203.29, -42.4) * mm, "end": v(-198.29, -37.4) * mm});
            skArc(sketch, "E106.2.endCap", {"start": v(-171.95, -37.4) * mm, "mid": v(-166.95, -42.4) * mm, "end": v(-171.95, -47.4) * mm});
            skLineSegment(sketch, "E106.2.left", {"start": v(-198.29, -37.4) * mm, "end": v(-171.95, -37.4) * mm});
            skLineSegment(sketch, "E106.2.right", {"start": v(-198.29, -47.4) * mm, "end": v(-171.95, -47.4) * mm});
            skArc(sketch, "E106.3.startCap", {"start": v(-158.95, -47.4) * mm, "mid": v(-163.95, -42.4) * mm, "end": v(-158.95, -37.4) * mm});
            skArc(sketch, "E106.3.endCap", {"start": v(-132.62, -37.4) * mm, "mid": v(-127.62, -42.4) * mm, "end": v(-132.62, -47.4) * mm});
            skLineSegment(sketch, "E106.3.left", {"start": v(-158.95, -37.4) * mm, "end": v(-132.62, -37.4) * mm});
            skLineSegment(sketch, "E106.3.right", {"start": v(-158.95, -47.4) * mm, "end": v(-132.62, -47.4) * mm});
            skArc(sketch, "E106.4.startCap", {"start": v(-119.62, -47.4) * mm, "mid": v(-124.62, -42.4) * mm, "end": v(-119.62, -37.4) * mm});
            skArc(sketch, "E106.4.endCap", {"start": v(-93.29, -37.4) * mm, "mid": v(-88.29, -42.4) * mm, "end": v(-93.29, -47.4) * mm});
            skLineSegment(sketch, "E106.4.left", {"start": v(-119.62, -37.4) * mm, "end": v(-93.29, -37.4) * mm});
            skLineSegment(sketch, "E106.4.right", {"start": v(-119.62, -47.4) * mm, "end": v(-93.29, -47.4) * mm});
            skArc(sketch, "E106.5.startCap", {"start": v(-188.29, -60.52) * mm, "mid": v(-193.29, -55.52) * mm, "end": v(-188.29, -50.52) * mm});
            skArc(sketch, "E106.5.endCap", {"start": v(-152.29, -50.52) * mm, "mid": v(-147.29, -55.52) * mm, "end": v(-152.29, -60.52) * mm});
            skLineSegment(sketch, "E106.5.left", {"start": v(-188.29, -50.52) * mm, "end": v(-152.29, -50.52) * mm});
            skLineSegment(sketch, "E106.5.right", {"start": v(-188.29, -60.52) * mm, "end": v(-152.29, -60.52) * mm});
            skArc(sketch, "E106.6.startCap", {"start": v(-139.29, -60.52) * mm, "mid": v(-144.29, -55.52) * mm, "end": v(-139.29, -50.52) * mm});
            skArc(sketch, "E106.6.endCap", {"start": v(-103.29, -50.52) * mm, "mid": v(-98.29, -55.52) * mm, "end": v(-103.29, -60.52) * mm});
            skLineSegment(sketch, "E106.6.left", {"start": v(-139.29, -50.52) * mm, "end": v(-103.29, -50.52) * mm});
            skLineSegment(sketch, "E106.6.right", {"start": v(-139.29, -60.52) * mm, "end": v(-103.29, -60.52) * mm});
            skCircle(sketch, "E107", {"center": v(-198.29, -55.52) * mm, "radius": 2.55 * mm});
            skCircle(sketch, "E108", {"center": v(-93.29, -55.52) * mm, "radius": 2.55 * mm});
            skLineSegment(sketch, "E109", {"start": v(-174.79, -137.52) * mm, "end": v(-166.79, -129.52) * mm});
            skLineSegment(sketch, "E110", {"start": v(-166.79, -129.52) * mm, "end": v(-84.79, -129.52) * mm});
            skLineSegment(sketch, "E111", {"start": v(-84.79, -129.52) * mm, "end": v(-76.79, -137.52) * mm});
            skLineSegment(sketch, "E112", {"start": v(-76.79, -137.52) * mm, "end": v(-174.79, -137.52) * mm});
            skSolve(sketch);
        }
        {
            var Q0;
            Q0=qSketchRegion(id+"F15",true);
            var Q1;
            {var subQ0=sQuery(id+"F15.wireOp",EDGE,"eD3hBwOG-1YSv-rIqv-KxOD-YYoGhDVYBiqk");Q1=makeQuery(id+"F15.imprint","IMPRINT",FACE,{"disambiguationData":[TD([[makeQuery(id+"F15.imprint","IMPRINT",EDGE,{"derivedFrom":subQ0}),-1.0]])]});}
            extrude(context, id + "F16", {"entities" : qUnion([Q0, Q1]), "operationType" : NewBodyOperationType.REMOVE, "oppositeDirection" : true, "depth" : 25 * mm});
        }
        {
            var Q0;
            Q0=qCreatedBy(makeId("Top.planeOp"),FACE);
            cPlane(context, id + "F17", {"entities" : qUnion([Q0]), "cplaneType" : CPlaneType.OFFSET, "offset" : 155 * mm, "width" : 150 * mm, "height" : 150 * mm});
        }
        {
            var Q0;
            Q0=qCreatedBy(id+"F17.planeOp",FACE);
            var sketch = newSketch(context, id + "F18", { "sketchPlane" : qUnion([Q0])});
            skLineSegment(sketch, "E113.bottom", {"start": v(-87.02, 155.87) * mm, "end": v(46.98, 155.87) * mm});
            skLineSegment(sketch, "E113.top", {"start": v(-87.02, 63.87) * mm, "end": v(46.98, 63.87) * mm});
            skLineSegment(sketch, "E113.left", {"start": v(-87.02, 155.87) * mm, "end": v(-87.02, 63.87) * mm});
            skLineSegment(sketch, "E113.right", {"start": v(46.98, 155.87) * mm, "end": v(46.98, 63.87) * mm});
            skLineSegment(sketch, "E114", {"start": v(-78.02, 63.87) * mm, "end": v(-83.02, 68.87) * mm});
            skLineSegment(sketch, "E115", {"start": v(37.98, 63.87) * mm, "end": v(42.98, 68.87) * mm});
            skLineSegment(sketch, "E116", {"start": v(-83.02, 68.87) * mm, "end": v(-87.02, 68.87) * mm});
            skLineSegment(sketch, "E117", {"start": v(42.98, 68.87) * mm, "end": v(46.98, 68.87) * mm});
            skLineSegment(sketch, "E118", {"start": v(36.98, 63.87) * mm, "end": v(36.98, 69.87) * mm, "construction": true});
            skCircle(sketch, "E119", {"center": v(36.98, 69.87) * mm, "radius": 1.6 * mm});
            skLineSegment(sketch, "E120", {"start": v(-77.02, 63.87) * mm, "end": v(-77.02, 69.87) * mm, "construction": true});
            skCircle(sketch, "E121", {"center": v(-77.02, 69.87) * mm, "radius": 1.6 * mm});
            skLineSegment(sketch, "E122", {"start": v(-53.02, 63.87) * mm, "end": v(-48.02, 68.87) * mm});
            skLineSegment(sketch, "E123", {"start": v(-48.02, 68.87) * mm, "end": v(7.98, 68.87) * mm});
            skLineSegment(sketch, "E124", {"start": v(7.98, 68.87) * mm, "end": v(12.98, 63.87) * mm});
            skSolve(sketch);
        }
        {
            var Q0;
            {var subQ1=sQuery(id+"F18.wireOp",EDGE,"E113.bottom");Q0=makeQuery(id+"F18.imprint","IMPRINT",FACE,{"disambiguationData":[TD([[makeQuery(id+"F18.imprint","IMPRINT",EDGE,{"derivedFrom":subQ1}),-1.0]])]});}
            extrude(context, id + "F19", {"entities" : qUnion([Q0]), "depth" : 3 * mm});
        }
        {
            var Q0;
            Q0=makeQuery(id+"F19.opExtrude","SWEPT_BODY",BODY,{"disambiguationData":[OSD([sQuery(id+"F18.wireOp",EDGE,"E113.bottom"),sQuery(id+"F18.wireOp",EDGE,"E113.top"),sQuery(id+"F18.wireOp",EDGE,"E113.left"),sQuery(id+"F18.wireOp",EDGE,"E113.right"),sQuery(id+"F18.wireOp",EDGE,"E114"),sQuery(id+"F18.wireOp",EDGE,"3zsQ1Kl9-2ynF-8LIN-0dku-r61PIn4XyDqG"),sQuery(id+"F18.wireOp",EDGE,"UXQkqX4z-jOis-0Iwp-P2ix-A9E3pHhtgsOQ"),sQuery(id+"F18.wireOp",EDGE,"E115"),sQuery(id+"F18.wireOp",EDGE,"LeDl9sKz-5wQR-wnus-53VY-3W6SMz2K6K2i"),sQuery(id+"F18.wireOp",EDGE,"1wH7Y6pB-1Br9-c6Mt-ri01-EdgmEcDOcEDC")])]});
            var Q1;
            Q1=makeQuery(id+"F19.opExtrude","SWEPT_FACE",FACE,{"disambiguationData":[OSD([sQuery(id+"F18.wireOp",EDGE,"E113.bottom")])]});
            mirror(context, id + "F20", {"operationType" : NewBodyOperationType.ADD, "entities" : qUnion([Q0]), "mirrorPlane" : qUnion([Q1])});
        }
        {
            var Q0;
            Q0=qCreatedBy(makeId("Top.planeOp"),FACE);
            cPlane(context, id + "F21", {"entities" : qUnion([Q0]), "cplaneType" : CPlaneType.OFFSET, "offset" : 153 * mm, "oppositeDirection" : true, "width" : 150 * mm, "height" : 150 * mm});
        }
        {
            var Q0;
            Q0=qCreatedBy(id+"F21.planeOp",FACE);
            var sketch = newSketch(context, id + "F22", { "sketchPlane" : qUnion([Q0])});
            skLineSegment(sketch, "E125.bottom", {"start": v(-72.92, 25.42) * mm, "end": v(61.08, 25.42) * mm});
            skLineSegment(sketch, "E125.top", {"start": v(-72.92, 117.42) * mm, "end": v(61.08, 117.42) * mm});
            skLineSegment(sketch, "E125.left", {"start": v(-72.92, 25.42) * mm, "end": v(-72.92, 117.42) * mm});
            skLineSegment(sketch, "E125.right", {"start": v(61.08, 25.42) * mm, "end": v(61.08, 117.42) * mm});
            skLineSegment(sketch, "E126", {"start": v(-63.92, 25.42) * mm, "end": v(-68.92, 30.42) * mm});
            skLineSegment(sketch, "E127", {"start": v(57.08, 30.42) * mm, "end": v(52.08, 25.42) * mm});
            skLineSegment(sketch, "E128", {"start": v(57.08, 30.42) * mm, "end": v(61.08, 30.42) * mm});
            skLineSegment(sketch, "E129", {"start": v(-68.92, 30.42) * mm, "end": v(-72.92, 30.42) * mm});
            skLineSegment(sketch, "E130", {"start": v(27.08, 25.42) * mm, "end": v(22.08, 30.42) * mm});
            skLineSegment(sketch, "E131", {"start": v(22.08, 30.42) * mm, "end": v(-33.92, 30.42) * mm});
            skLineSegment(sketch, "E132", {"start": v(-33.92, 30.42) * mm, "end": v(-38.92, 25.42) * mm});
            skLineSegment(sketch, "E133", {"start": v(-62.92, 25.42) * mm, "end": v(-62.92, 31.42) * mm, "construction": true});
            skCircle(sketch, "E134", {"center": v(-62.92, 31.42) * mm, "radius": 1.6 * mm});
            skLineSegment(sketch, "E135", {"start": v(51.08, 25.42) * mm, "end": v(51.08, 31.42) * mm, "construction": true});
            skCircle(sketch, "E136", {"center": v(51.08, 31.42) * mm, "radius": 1.6 * mm});
            skSolve(sketch);
        }
        {
            var Q0;
            {var subQ1=sQuery(id+"F22.wireOp",EDGE,"E125.top");Q0=makeQuery(id+"F22.imprint","IMPRINT",FACE,{"disambiguationData":[TD([[makeQuery(id+"F22.imprint","IMPRINT",EDGE,{"derivedFrom":subQ1}),-1.0]])]});}
            extrude(context, id + "F23", {"entities" : qUnion([Q0]), "depth" : 3 * mm});
        }
        {
            var Q0;
            Q0=makeQuery(id+"F23.opExtrude","SWEPT_BODY",BODY,{"disambiguationData":[OSD([sQuery(id+"F22.wireOp",EDGE,"E125.bottom"),sQuery(id+"F22.wireOp",EDGE,"E125.top"),sQuery(id+"F22.wireOp",EDGE,"E125.left"),sQuery(id+"F22.wireOp",EDGE,"E125.right"),sQuery(id+"F22.wireOp",EDGE,"E126"),sQuery(id+"F22.wireOp",EDGE,"dnEH7a7q-0e2G-ZF1u-gQp3-ZGx2YlrUhsfq"),sQuery(id+"F22.wireOp",EDGE,"EYcrjZ5U-B8Tu-Hvld-BROV-cSRqyUUC4nfP"),sQuery(id+"F22.wireOp",EDGE,"lcQWckg9-mZXk-lsL4-PW7S-RH1iYC4EfrxX"),sQuery(id+"F22.wireOp",EDGE,"m4YSihPu-nfU7-MdAm-Gg2Q-VAeN7eaJ9XWN"),sQuery(id+"F22.wireOp",EDGE,"E127")])]});
            var Q1;
            Q1=makeQuery(id+"F23.opExtrude","SWEPT_FACE",FACE,{"disambiguationData":[OSD([sQuery(id+"F22.wireOp",EDGE,"E125.top")])]});
            mirror(context, id + "F24", {"operationType" : NewBodyOperationType.ADD, "entities" : qUnion([Q0]), "mirrorPlane" : qUnion([Q1])});
        }
        {
            var Q0;
            Q0=qCreatedBy(makeId("Front.planeOp"),FACE);
            cPlane(context, id + "F25", {"entities" : qUnion([Q0]), "cplaneType" : CPlaneType.OFFSET, "offset" : 376 * mm, "oppositeDirection" : true, "width" : 150 * mm, "height" : 150 * mm});
        }
        {
            var Q0;
            Q0=qCreatedBy(id+"F25.planeOp",FACE);
            var sketch = newSketch(context, id + "F26", { "sketchPlane" : qUnion([Q0])});
            skLineSegment(sketch, "E137.bottom", {"start": v(-68, 122.5) * mm, "end": v(66, 122.5) * mm});
            skLineSegment(sketch, "E137.top", {"start": v(-68, 8.5) * mm, "end": v(66, 8.5) * mm});
            skLineSegment(sketch, "E137.left", {"start": v(-68, 122.5) * mm, "end": v(-68, 8.5) * mm});
            skLineSegment(sketch, "E137.right", {"start": v(66, 122.5) * mm, "end": v(66, 8.5) * mm});
            skLineSegment(sketch, "E138", {"start": v(-68, 113.5) * mm, "end": v(-64, 113.5) * mm});
            skLineSegment(sketch, "E139", {"start": v(-64, 113.5) * mm, "end": v(-59, 118.5) * mm});
            skLineSegment(sketch, "E140", {"start": v(56, 122.5) * mm, "end": v(56, 112.5) * mm, "construction": true});
            skCircle(sketch, "E141", {"center": v(56, 112.5) * mm, "radius": 1.6 * mm});
            skLineSegment(sketch, "E142", {"start": v(-58, 122.5) * mm, "end": v(-58, 112.5) * mm, "construction": true});
            skCircle(sketch, "E143", {"center": v(-58, 112.5) * mm, "radius": 1.6 * mm});
            skLineSegment(sketch, "E144", {"start": v(66, 113.5) * mm, "end": v(62, 113.5) * mm});
            skLineSegment(sketch, "E145", {"start": v(62, 113.5) * mm, "end": v(57, 118.5) * mm});
            skLineSegment(sketch, "E146", {"start": v(57, 118.5) * mm, "end": v(-59, 118.5) * mm});
            skSolve(sketch);
        }
        {
            var Q0;
            {var subQ1=sQuery(id+"F26.wireOp",EDGE,"E137.top");Q0=makeQuery(id+"F26.imprint","IMPRINT",FACE,{"disambiguationData":[TD([[makeQuery(id+"F26.imprint","IMPRINT",EDGE,{"derivedFrom":subQ1}),1.0]])]});}
            extrude(context, id + "F27", {"entities" : qUnion([Q0]), "depth" : 3 * mm});
        }
        {
            var Q0;
            Q0=makeQuery(id+"F27.opExtrude","SWEPT_BODY",BODY,{"disambiguationData":[OSD([sQuery(id+"F26.wireOp",EDGE,"E137.bottom"),sQuery(id+"F26.wireOp",EDGE,"E137.top"),sQuery(id+"F26.wireOp",EDGE,"E137.left"),sQuery(id+"F26.wireOp",EDGE,"E137.right"),sQuery(id+"F26.wireOp",EDGE,"E138"),sQuery(id+"F26.wireOp",EDGE,"E139"),sQuery(id+"F26.wireOp",EDGE,"ccf2e9e3-9b64-4f2a-9f18-310bc790516a"),sQuery(id+"F26.wireOp",EDGE,"c5f426b9-73f2-4868-9408-4cfd947a191f"),sQuery(id+"F26.wireOp",EDGE,"cd8d91dd-9a42-4ae4-8430-5a7eccad3886"),sQuery(id+"F26.wireOp",EDGE,"f1dcae7c-8bd8-43e5-b7b1-ff3532f110ef")])]});
            var Q1;
            Q1=makeQuery(id+"F27.opExtrude","SWEPT_FACE",FACE,{"disambiguationData":[OSD([sQuery(id+"F26.wireOp",EDGE,"E137.top")])]});
            mirror(context, id + "F28", {"operationType" : NewBodyOperationType.ADD, "entities" : qUnion([Q0]), "mirrorPlane" : qUnion([Q1])});
        }
        {
            var Q0;
            {var subQ0=makeQuery(id+"F27.opExtrude","CAP_FACE",FACE,{"disambiguationData":[OSD([sQuery(id+"F26.wireOp",EDGE,"E137.bottom"),sQuery(id+"F26.wireOp",EDGE,"E137.top"),sQuery(id+"F26.wireOp",EDGE,"E137.left"),sQuery(id+"F26.wireOp",EDGE,"E137.right"),sQuery(id+"F26.wireOp",EDGE,"E138"),sQuery(id+"F26.wireOp",EDGE,"E139"),sQuery(id+"F26.wireOp",EDGE,"ccf2e9e3-9b64-4f2a-9f18-310bc790516a"),sQuery(id+"F26.wireOp",EDGE,"c5f426b9-73f2-4868-9408-4cfd947a191f"),sQuery(id+"F26.wireOp",EDGE,"cd8d91dd-9a42-4ae4-8430-5a7eccad3886"),sQuery(id+"F26.wireOp",EDGE,"f1dcae7c-8bd8-43e5-b7b1-ff3532f110ef")])],"isStart":true});Q0=makeQuery(id+"F28.boolean.opBoolean","MERGE",FACE,{"derivedFrom":[subQ0,makeQuery(id+"F28.opPattern","COPY",FACE,{"derivedFrom":subQ0,"instanceName":"1"})]});}
            var sketch = newSketch(context, id + "F29", { "sketchPlane" : qUnion([Q0])});
            skLineSegment(sketch, "E147", {"start": v(-55, 104.5) * mm, "end": v(-55, -65.5) * mm, "construction": true});
            skLineSegment(sketch, "E148", {"start": v(-55, -65.5) * mm, "end": v(-66, -65.5) * mm, "construction": true});
            skLineSegment(sketch, "E149", {"start": v(-55, -64.2) * mm, "end": v(-46.9, -64.2) * mm, "construction": true});
            skLineSegment(sketch, "E150.bottom", {"start": v(-46.9, -72.15) * mm, "end": v(49.5, -72.15) * mm});
            skLineSegment(sketch, "E150.top", {"start": v(-46.9, -56.25) * mm, "end": v(49.5, -56.25) * mm});
            skLineSegment(sketch, "E150.left", {"start": v(-46.9, -72.15) * mm, "end": v(-46.9, -56.25) * mm});
            skLineSegment(sketch, "E150.right", {"start": v(49.5, -72.15) * mm, "end": v(49.5, -56.25) * mm});
            skLineSegment(sketch, "E151.bottom", {"start": v(-46.9, -76.55) * mm, "end": v(49.5, -76.55) * mm});
            skLineSegment(sketch, "E151.top", {"start": v(-46.9, -92.45) * mm, "end": v(49.5, -92.45) * mm});
            skLineSegment(sketch, "E151.left", {"start": v(-46.9, -76.55) * mm, "end": v(-46.9, -92.45) * mm});
            skLineSegment(sketch, "E151.right", {"start": v(49.5, -76.55) * mm, "end": v(49.5, -92.45) * mm});
            skLineSegment(sketch, "E152", {"start": v(49.5, -76.55) * mm, "end": v(49.5, -72.15) * mm, "construction": true});
            skLineSegment(sketch, "E153.bottom", {"start": v(-12.6, 107.1) * mm, "end": v(-57.3, 107.1) * mm});
            skLineSegment(sketch, "E154", {"start": v(-57.3, 107.1) * mm, "end": v(-57.3, -51.9) * mm});
            skLineSegment(sketch, "E155", {"start": v(-57.3, -51.9) * mm, "end": v(-12.6, -51.9) * mm});
            skLineSegment(sketch, "E156", {"start": v(-12.6, -51.9) * mm, "end": v(-12.6, 107.1) * mm});
            skArc(sketch, "E157", {"start": v(-56.55, 107.1) * mm, "mid": v(-57.83, 107.63) * mm, "end": v(-57.3, 106.35) * mm});
            skArc(sketch, "E158", {"start": v(-12.6, 106.35) * mm, "mid": v(-12.07, 107.63) * mm, "end": v(-13.35, 107.1) * mm});
            skArc(sketch, "E159", {"start": v(-57.3, -51.15) * mm, "mid": v(-57.83, -52.43) * mm, "end": v(-56.55, -51.9) * mm});
            skLineSegment(sketch, "E160", {"start": v(54.5, -51.75) * mm, "end": v(54.5, -91.75) * mm});
            skLineSegment(sketch, "E161", {"start": v(49.5, -56.25) * mm, "end": v(54.5, -56.25) * mm, "construction": true});
            skLineSegment(sketch, "E162", {"start": v(54.5, -91.75) * mm, "end": v(72.5, -91.75) * mm});
            skLineSegment(sketch, "E163", {"start": v(-57, -101.5) * mm, "end": v(-66, -101.5) * mm, "construction": true});
            skLineSegment(sketch, "E164", {"start": v(72.5, -51.75) * mm, "end": v(72.5, -91.75) * mm});
            skLineSegment(sketch, "E165", {"start": v(54.5, -51.75) * mm, "end": v(60.5, -51.75) * mm});
            skLineSegment(sketch, "E166", {"start": v(60.5, -51.75) * mm, "end": v(63.5, -48.75) * mm});
            skLineSegment(sketch, "E167", {"start": v(63.5, -48.75) * mm, "end": v(72.5, -48.75) * mm});
            skLineSegment(sketch, "E168", {"start": v(72.5, -48.75) * mm, "end": v(72.5, -51.75) * mm});
            skLineSegment(sketch, "E169", {"start": v(60.5, -51.75) * mm, "end": v(72.5, -51.75) * mm, "construction": true});
            skArc(sketch, "E170", {"start": v(-13.35, -51.9) * mm, "mid": v(-12.07, -52.43) * mm, "end": v(-12.6, -51.15) * mm});
            skSolve(sketch);
        }
        {
            var Q0;
            {var subQ0=makeQuery(id+"F27.opExtrude","CAP_FACE",FACE,{"disambiguationData":[OSD([sQuery(id+"F26.wireOp",EDGE,"E137.bottom"),sQuery(id+"F26.wireOp",EDGE,"E137.top"),sQuery(id+"F26.wireOp",EDGE,"E137.left"),sQuery(id+"F26.wireOp",EDGE,"E137.right"),sQuery(id+"F26.wireOp",EDGE,"E138"),sQuery(id+"F26.wireOp",EDGE,"E139"),sQuery(id+"F26.wireOp",EDGE,"ccf2e9e3-9b64-4f2a-9f18-310bc790516a"),sQuery(id+"F26.wireOp",EDGE,"c5f426b9-73f2-4868-9408-4cfd947a191f"),sQuery(id+"F26.wireOp",EDGE,"cd8d91dd-9a42-4ae4-8430-5a7eccad3886"),sQuery(id+"F26.wireOp",EDGE,"f1dcae7c-8bd8-43e5-b7b1-ff3532f110ef")])],"isStart":true});Q0=makeQuery(id+"F28.boolean.opBoolean","MERGE",FACE,{"derivedFrom":[subQ0,makeQuery(id+"F28.opPattern","COPY",FACE,{"derivedFrom":subQ0,"instanceName":"1"})]});}
            var sketch = newSketch(context, id + "F30", { "sketchPlane" : qUnion([Q0])});
            skLineSegment(sketch, "E171", {"start": v(4.25, 66.5) * mm, "end": v(4.25, 42.5) * mm, "construction": true});
            skLineSegment(sketch, "E172", {"start": v(4.25, 42.5) * mm, "end": v(4.25, 27.5) * mm, "construction": true});
            skLineSegment(sketch, "E173", {"start": v(4.25, 27.5) * mm, "end": v(4.25, 3.5) * mm, "construction": true});
            skLineSegment(sketch, "E174", {"start": v(4.25, 3.5) * mm, "end": v(4.25, -11.5) * mm, "construction": true});
            skLineSegment(sketch, "E175", {"start": v(4.25, -11.5) * mm, "end": v(4.25, -35.5) * mm, "construction": true});
            skArc(sketch, "E176.0.startCap", {"start": v(0.25, 66.5) * mm, "mid": v(4.25, 70.5) * mm, "end": v(8.25, 66.5) * mm});
            skArc(sketch, "E176.0.endCap", {"start": v(8.25, 42.5) * mm, "mid": v(4.25, 38.5) * mm, "end": v(0.25, 42.5) * mm});
            skLineSegment(sketch, "E176.0.left", {"start": v(8.25, 66.5) * mm, "end": v(8.25, 42.5) * mm});
            skLineSegment(sketch, "E176.0.right", {"start": v(0.25, 66.5) * mm, "end": v(0.25, 42.5) * mm});
            skArc(sketch, "E176.1.startCap", {"start": v(0.25, 27.5) * mm, "mid": v(4.25, 31.5) * mm, "end": v(8.25, 27.5) * mm});
            skArc(sketch, "E176.1.endCap", {"start": v(8.25, 3.5) * mm, "mid": v(4.25, -0.5) * mm, "end": v(0.25, 3.5) * mm});
            skLineSegment(sketch, "E176.1.left", {"start": v(8.25, 27.5) * mm, "end": v(8.25, 3.5) * mm});
            skLineSegment(sketch, "E176.1.right", {"start": v(0.25, 27.5) * mm, "end": v(0.25, 3.5) * mm});
            skArc(sketch, "E176.2.startCap", {"start": v(0.25, -11.5) * mm, "mid": v(4.25, -7.5) * mm, "end": v(8.25, -11.5) * mm});
            skArc(sketch, "E176.2.endCap", {"start": v(8.25, -35.5) * mm, "mid": v(4.25, -39.5) * mm, "end": v(0.25, -35.5) * mm});
            skLineSegment(sketch, "E176.2.left", {"start": v(8.25, -11.5) * mm, "end": v(8.25, -35.5) * mm});
            skLineSegment(sketch, "E176.2.right", {"start": v(0.25, -11.5) * mm, "end": v(0.25, -35.5) * mm});
            skLineSegment(sketch, "E177.1.0.0", {"start": v(16.25, 27.5) * mm, "end": v(16.25, 3.5) * mm});
            skArc(sketch, "E177.1.0.1", {"start": v(16.25, -11.5) * mm, "mid": v(20.25, -7.5) * mm, "end": v(24.25, -11.5) * mm});
            skArc(sketch, "E177.1.0.3", {"start": v(16.25, 66.5) * mm, "mid": v(20.25, 70.5) * mm, "end": v(24.25, 66.5) * mm});
            skLineSegment(sketch, "E177.1.0.4", {"start": v(16.25, -11.5) * mm, "end": v(16.25, -35.5) * mm});
            skArc(sketch, "E177.1.0.5", {"start": v(16.25, 27.5) * mm, "mid": v(20.25, 31.5) * mm, "end": v(24.25, 27.5) * mm});
            skArc(sketch, "E177.1.0.6", {"start": v(24.25, -35.5) * mm, "mid": v(20.25, -39.5) * mm, "end": v(16.25, -35.5) * mm});
            skArc(sketch, "E177.1.0.7", {"start": v(24.25, 3.5) * mm, "mid": v(20.25, -0.5) * mm, "end": v(16.25, 3.5) * mm});
            skLineSegment(sketch, "E177.1.0.11", {"start": v(20.25, -11.5) * mm, "end": v(20.25, -35.5) * mm, "construction": true});
            skLineSegment(sketch, "E177.1.0.12", {"start": v(20.25, 3.5) * mm, "end": v(20.25, -11.5) * mm, "construction": true});
            skLineSegment(sketch, "E177.1.0.13", {"start": v(20.25, 27.5) * mm, "end": v(20.25, 3.5) * mm, "construction": true});
            skLineSegment(sketch, "E177.1.0.14", {"start": v(20.25, 42.5) * mm, "end": v(20.25, 27.5) * mm, "construction": true});
            skLineSegment(sketch, "E177.1.0.15", {"start": v(20.25, 66.5) * mm, "end": v(20.25, 42.5) * mm, "construction": true});
            skLineSegment(sketch, "E177.1.0.16", {"start": v(24.25, 27.5) * mm, "end": v(24.25, 3.5) * mm});
            skLineSegment(sketch, "E177.1.0.20", {"start": v(16.25, 66.5) * mm, "end": v(16.25, 42.5) * mm});
            skLineSegment(sketch, "E177.1.0.21", {"start": v(24.25, 66.5) * mm, "end": v(24.25, 42.5) * mm});
            skArc(sketch, "E177.1.0.22", {"start": v(24.25, 42.5) * mm, "mid": v(20.25, 38.5) * mm, "end": v(16.25, 42.5) * mm});
            skLineSegment(sketch, "E177.1.0.23", {"start": v(24.25, -11.5) * mm, "end": v(24.25, -35.5) * mm});
            skLineSegment(sketch, "E177.2.0.0", {"start": v(32.25, 27.5) * mm, "end": v(32.25, 3.5) * mm});
            skArc(sketch, "E177.2.0.1", {"start": v(32.25, -11.5) * mm, "mid": v(36.25, -7.5) * mm, "end": v(40.25, -11.5) * mm});
            skArc(sketch, "E177.2.0.3", {"start": v(32.25, 66.5) * mm, "mid": v(36.25, 70.5) * mm, "end": v(40.25, 66.5) * mm});
            skLineSegment(sketch, "E177.2.0.4", {"start": v(32.25, -11.5) * mm, "end": v(32.25, -35.5) * mm});
            skArc(sketch, "E177.2.0.5", {"start": v(32.25, 27.5) * mm, "mid": v(36.25, 31.5) * mm, "end": v(40.25, 27.5) * mm});
            skArc(sketch, "E177.2.0.6", {"start": v(40.25, -35.5) * mm, "mid": v(36.25, -39.5) * mm, "end": v(32.25, -35.5) * mm});
            skArc(sketch, "E177.2.0.7", {"start": v(40.25, 3.5) * mm, "mid": v(36.25, -0.5) * mm, "end": v(32.25, 3.5) * mm});
            skLineSegment(sketch, "E177.2.0.11", {"start": v(36.25, -11.5) * mm, "end": v(36.25, -35.5) * mm, "construction": true});
            skLineSegment(sketch, "E177.2.0.12", {"start": v(36.25, 3.5) * mm, "end": v(36.25, -11.5) * mm, "construction": true});
            skLineSegment(sketch, "E177.2.0.13", {"start": v(36.25, 27.5) * mm, "end": v(36.25, 3.5) * mm, "construction": true});
            skLineSegment(sketch, "E177.2.0.14", {"start": v(36.25, 42.5) * mm, "end": v(36.25, 27.5) * mm, "construction": true});
            skLineSegment(sketch, "E177.2.0.15", {"start": v(36.25, 66.5) * mm, "end": v(36.25, 42.5) * mm, "construction": true});
            skLineSegment(sketch, "E177.2.0.16", {"start": v(40.25, 27.5) * mm, "end": v(40.25, 3.5) * mm});
            skLineSegment(sketch, "E177.2.0.20", {"start": v(32.25, 66.5) * mm, "end": v(32.25, 42.5) * mm});
            skLineSegment(sketch, "E177.2.0.21", {"start": v(40.25, 66.5) * mm, "end": v(40.25, 42.5) * mm});
            skArc(sketch, "E177.2.0.22", {"start": v(40.25, 42.5) * mm, "mid": v(36.25, 38.5) * mm, "end": v(32.25, 42.5) * mm});
            skLineSegment(sketch, "E177.2.0.23", {"start": v(40.25, -11.5) * mm, "end": v(40.25, -35.5) * mm});
            skLineSegment(sketch, "E177.direction1", {"start": v(0.25, -35.5) * mm, "end": v(16.25, -35.5) * mm, "construction": true});
            skLineSegment(sketch, "E178", {"start": v(48, 96.85) * mm, "end": v(68, 96.85) * mm, "construction": true});
            skCircle(sketch, "E179", {"center": v(48, 96.85) * mm, "radius": 6 * mm});
            skLineSegment(sketch, "E180.bottom", {"start": v(-5.75, 108.1) * mm, "end": v(21.75, 108.1) * mm});
            skLineSegment(sketch, "E180.top", {"start": v(-5.75, 85.6) * mm, "end": v(21.75, 85.6) * mm});
            skLineSegment(sketch, "E180.left", {"start": v(-7.75, 106.1) * mm, "end": v(-7.75, 87.6) * mm});
            skLineSegment(sketch, "E180.right", {"start": v(23.75, 106.1) * mm, "end": v(23.75, 87.6) * mm});
            skLineSegment(sketch, "E181", {"start": v(8, 108.1) * mm, "end": v(8, 118.5) * mm, "construction": true});
            skLineSegment(sketch, "E182", {"start": v(-7.75, 96.85) * mm, "end": v(-12, 96.85) * mm, "construction": true});
            skLineSegment(sketch, "E183", {"start": v(23.75, 96.85) * mm, "end": v(28, 96.85) * mm, "construction": true});
            skCircle(sketch, "E184", {"center": v(-12, 96.85) * mm, "radius": 1.6 * mm});
            skCircle(sketch, "E185", {"center": v(28, 96.85) * mm, "radius": 1.6 * mm});
            skPoint(sketch, "E186.visualSharp", {"position": v(-7.75, 108.1) * mm});
            skArc(sketch, "E186.filletArc", {"start": v(-5.75, 108.1) * mm, "mid": v(-7.16, 107.51) * mm, "end": v(-7.75, 106.1) * mm});
            skPoint(sketch, "E187.visualSharp", {"position": v(23.75, 108.1) * mm});
            skArc(sketch, "E187.filletArc", {"start": v(23.75, 106.1) * mm, "mid": v(23.16, 107.51) * mm, "end": v(21.75, 108.1) * mm});
            skPoint(sketch, "E188.visualSharp", {"position": v(-7.75, 85.6) * mm});
            skArc(sketch, "E188.filletArc", {"start": v(-7.75, 87.6) * mm, "mid": v(-7.16, 86.18) * mm, "end": v(-5.75, 85.6) * mm});
            skPoint(sketch, "E189.visualSharp", {"position": v(23.75, 85.6) * mm});
            skArc(sketch, "E189.filletArc", {"start": v(21.75, 85.6) * mm, "mid": v(23.16, 86.18) * mm, "end": v(23.75, 87.6) * mm});
            skLineSegment(sketch, "E190", {"start": v(28, 96.85) * mm, "end": v(48, 96.85) * mm, "construction": true});
            skLineSegment(sketch, "E191", {"start": v(4.25, -35.5) * mm, "end": v(-66, -35.5) * mm, "construction": true});
            skSolve(sketch);
        }
        {
            var Q0;
            Q0=qSketchRegion(id+"F29",true);
            var Q1;
            Q1=qSketchRegion(id+"F30",true);
            extrude(context, id + "F31", {"entities" : qUnion([Q0, Q1]), "operationType" : NewBodyOperationType.REMOVE, "oppositeDirection" : true, "depth" : 25 * mm});
        }
        {
            var Q0;
            Q0=makeQuery(id+"F31.boolean.opBoolean","COPY",EDGE,{"derivedFrom":makeQuery(id+"F31.opExtrude","SWEPT_EDGE",EDGE,{"disambiguationData":[OSD([sQuery(id+"F29.wireOp",EDGE,"E150.top"),sQuery(id+"F29.wireOp",EDGE,"E150.left")])]})});
            var Q1;
            Q1=makeQuery(id+"F31.boolean.opBoolean","COPY",EDGE,{"derivedFrom":makeQuery(id+"F31.opExtrude","SWEPT_EDGE",EDGE,{"disambiguationData":[OSD([sQuery(id+"F29.wireOp",EDGE,"E150.bottom"),sQuery(id+"F29.wireOp",EDGE,"E150.left")])]})});
            var Q2;
            Q2=makeQuery(id+"F31.boolean.opBoolean","COPY",EDGE,{"derivedFrom":makeQuery(id+"F31.opExtrude","SWEPT_EDGE",EDGE,{"disambiguationData":[OSD([sQuery(id+"F29.wireOp",EDGE,"E151.bottom"),sQuery(id+"F29.wireOp",EDGE,"E151.left")])]})});
            var Q3;
            Q3=makeQuery(id+"F31.boolean.opBoolean","COPY",EDGE,{"derivedFrom":makeQuery(id+"F31.opExtrude","SWEPT_EDGE",EDGE,{"disambiguationData":[OSD([sQuery(id+"F29.wireOp",EDGE,"E151.top"),sQuery(id+"F29.wireOp",EDGE,"E151.left")])]})});
            var Q4;
            Q4=makeQuery(id+"F31.boolean.opBoolean","COPY",EDGE,{"derivedFrom":makeQuery(id+"F31.opExtrude","SWEPT_EDGE",EDGE,{"disambiguationData":[OSD([sQuery(id+"F29.wireOp",EDGE,"E151.top"),sQuery(id+"F29.wireOp",EDGE,"E151.right")])]})});
            var Q5;
            Q5=makeQuery(id+"F31.boolean.opBoolean","COPY",EDGE,{"derivedFrom":makeQuery(id+"F31.opExtrude","SWEPT_EDGE",EDGE,{"disambiguationData":[OSD([sQuery(id+"F29.wireOp",EDGE,"E151.bottom"),sQuery(id+"F29.wireOp",EDGE,"E151.right")])]})});
            var Q6;
            Q6=makeQuery(id+"F31.boolean.opBoolean","COPY",EDGE,{"derivedFrom":makeQuery(id+"F31.opExtrude","SWEPT_EDGE",EDGE,{"disambiguationData":[OSD([sQuery(id+"F29.wireOp",EDGE,"E150.bottom"),sQuery(id+"F29.wireOp",EDGE,"E150.right")])]})});
            var Q7;
            Q7=makeQuery(id+"F31.boolean.opBoolean","COPY",EDGE,{"derivedFrom":makeQuery(id+"F31.opExtrude","SWEPT_EDGE",EDGE,{"disambiguationData":[OSD([sQuery(id+"F29.wireOp",EDGE,"E150.top"),sQuery(id+"F29.wireOp",EDGE,"E150.right")])]})});
            chamfer(context, id + "F32", {"entities" : qUnion([Q0, Q1, Q2, Q3, Q4, Q5, Q6, Q7]), "width" : 2 * mm, "tangentPropagation" : true});
        }
        {
            var Q0;
            {var subQ0=makeQuery(id+"F19.opExtrude","CAP_FACE",FACE,{"disambiguationData":[OSD([sQuery(id+"F18.wireOp",EDGE,"E113.bottom"),sQuery(id+"F18.wireOp",EDGE,"E113.top"),sQuery(id+"F18.wireOp",EDGE,"E113.left"),sQuery(id+"F18.wireOp",EDGE,"E113.right"),sQuery(id+"F18.wireOp",EDGE,"E114"),sQuery(id+"F18.wireOp",EDGE,"E115"),sQuery(id+"F18.wireOp",EDGE,"E116"),sQuery(id+"F18.wireOp",EDGE,"E117")])],"isStart":false});Q0=makeQuery(id+"F20.boolean.opBoolean","MERGE",FACE,{"derivedFrom":[subQ0,makeQuery(id+"F20.opPattern","COPY",FACE,{"derivedFrom":subQ0,"instanceName":"1"})]});}
            var sketch = newSketch(context, id + "F33", { "sketchPlane" : qUnion([Q0])});
            skLineSegment(sketch, "E192", {"start": v(17.98, 247.87) * mm, "end": v(17.98, 224.62) * mm, "construction": true});
            skLineSegment(sketch, "E193", {"start": v(17.98, 224.62) * mm, "end": v(32.98, 224.62) * mm, "construction": true});
            skArc(sketch, "E194.0.startCap", {"start": v(17.98, 222.12) * mm, "mid": v(15.48, 224.62) * mm, "end": v(17.98, 227.12) * mm});
            skArc(sketch, "E194.0.endCap", {"start": v(32.98, 227.12) * mm, "mid": v(35.48, 224.62) * mm, "end": v(32.98, 222.12) * mm});
            skLineSegment(sketch, "E194.0.left", {"start": v(17.98, 227.12) * mm, "end": v(32.98, 227.12) * mm});
            skLineSegment(sketch, "E194.0.right", {"start": v(17.98, 222.12) * mm, "end": v(32.98, 222.12) * mm});
            skLineSegment(sketch, "E195.0.1.0", {"start": v(17.98, 212.12) * mm, "end": v(32.98, 212.12) * mm});
            skLineSegment(sketch, "E195.0.1.1", {"start": v(17.98, 217.12) * mm, "end": v(32.98, 217.12) * mm});
            skArc(sketch, "E195.0.1.2", {"start": v(17.98, 212.12) * mm, "mid": v(15.48, 214.62) * mm, "end": v(17.98, 217.12) * mm});
            skLineSegment(sketch, "E195.0.1.3", {"start": v(17.98, 214.62) * mm, "end": v(32.98, 214.62) * mm, "construction": true});
            skArc(sketch, "E195.0.1.4", {"start": v(32.98, 217.12) * mm, "mid": v(35.48, 214.62) * mm, "end": v(32.98, 212.12) * mm});
            skLineSegment(sketch, "E195.0.2.0", {"start": v(17.98, 202.12) * mm, "end": v(32.98, 202.12) * mm});
            skLineSegment(sketch, "E195.0.2.1", {"start": v(17.98, 207.12) * mm, "end": v(32.98, 207.12) * mm});
            skArc(sketch, "E195.0.2.2", {"start": v(17.98, 202.12) * mm, "mid": v(15.48, 204.62) * mm, "end": v(17.98, 207.12) * mm});
            skLineSegment(sketch, "E195.0.2.3", {"start": v(17.98, 204.62) * mm, "end": v(32.98, 204.62) * mm, "construction": true});
            skArc(sketch, "E195.0.2.4", {"start": v(32.98, 207.12) * mm, "mid": v(35.48, 204.62) * mm, "end": v(32.98, 202.12) * mm});
            skLineSegment(sketch, "E195.0.3.0", {"start": v(17.98, 192.12) * mm, "end": v(32.98, 192.12) * mm});
            skLineSegment(sketch, "E195.0.3.1", {"start": v(17.98, 197.12) * mm, "end": v(32.98, 197.12) * mm});
            skArc(sketch, "E195.0.3.2", {"start": v(17.98, 192.12) * mm, "mid": v(15.48, 194.62) * mm, "end": v(17.98, 197.12) * mm});
            skLineSegment(sketch, "E195.0.3.3", {"start": v(17.98, 194.62) * mm, "end": v(32.98, 194.62) * mm, "construction": true});
            skArc(sketch, "E195.0.3.4", {"start": v(32.98, 197.12) * mm, "mid": v(35.48, 194.62) * mm, "end": v(32.98, 192.12) * mm});
            skLineSegment(sketch, "E195.0.4.0", {"start": v(17.98, 182.12) * mm, "end": v(32.98, 182.12) * mm});
            skLineSegment(sketch, "E195.0.4.1", {"start": v(17.98, 187.12) * mm, "end": v(32.98, 187.12) * mm});
            skArc(sketch, "E195.0.4.2", {"start": v(17.98, 182.12) * mm, "mid": v(15.48, 184.62) * mm, "end": v(17.98, 187.12) * mm});
            skLineSegment(sketch, "E195.0.4.3", {"start": v(17.98, 184.62) * mm, "end": v(32.98, 184.62) * mm, "construction": true});
            skArc(sketch, "E195.0.4.4", {"start": v(32.98, 187.12) * mm, "mid": v(35.48, 184.62) * mm, "end": v(32.98, 182.12) * mm});
            skLineSegment(sketch, "E195.0.5.0", {"start": v(17.98, 172.12) * mm, "end": v(32.98, 172.12) * mm});
            skLineSegment(sketch, "E195.0.5.1", {"start": v(17.98, 177.12) * mm, "end": v(32.98, 177.12) * mm});
            skArc(sketch, "E195.0.5.2", {"start": v(17.98, 172.12) * mm, "mid": v(15.48, 174.62) * mm, "end": v(17.98, 177.12) * mm});
            skLineSegment(sketch, "E195.0.5.3", {"start": v(17.98, 174.62) * mm, "end": v(32.98, 174.62) * mm, "construction": true});
            skArc(sketch, "E195.0.5.4", {"start": v(32.98, 177.12) * mm, "mid": v(35.48, 174.62) * mm, "end": v(32.98, 172.12) * mm});
            skLineSegment(sketch, "E195.0.6.0", {"start": v(17.98, 162.12) * mm, "end": v(32.98, 162.12) * mm});
            skLineSegment(sketch, "E195.0.6.1", {"start": v(17.98, 167.12) * mm, "end": v(32.98, 167.12) * mm});
            skArc(sketch, "E195.0.6.2", {"start": v(17.98, 162.12) * mm, "mid": v(15.48, 164.62) * mm, "end": v(17.98, 167.12) * mm});
            skLineSegment(sketch, "E195.0.6.3", {"start": v(17.98, 164.62) * mm, "end": v(32.98, 164.62) * mm, "construction": true});
            skArc(sketch, "E195.0.6.4", {"start": v(32.98, 167.12) * mm, "mid": v(35.48, 164.62) * mm, "end": v(32.98, 162.12) * mm});
            skLineSegment(sketch, "E195.0.7.0", {"start": v(17.98, 152.12) * mm, "end": v(32.98, 152.12) * mm});
            skLineSegment(sketch, "E195.0.7.1", {"start": v(17.98, 157.12) * mm, "end": v(32.98, 157.12) * mm});
            skArc(sketch, "E195.0.7.2", {"start": v(17.98, 152.12) * mm, "mid": v(15.48, 154.62) * mm, "end": v(17.98, 157.12) * mm});
            skLineSegment(sketch, "E195.0.7.3", {"start": v(17.98, 154.62) * mm, "end": v(32.98, 154.62) * mm, "construction": true});
            skArc(sketch, "E195.0.7.4", {"start": v(32.98, 157.12) * mm, "mid": v(35.48, 154.62) * mm, "end": v(32.98, 152.12) * mm});
            skLineSegment(sketch, "E195.0.8.0", {"start": v(17.98, 142.12) * mm, "end": v(32.98, 142.12) * mm});
            skLineSegment(sketch, "E195.0.8.1", {"start": v(17.98, 147.12) * mm, "end": v(32.98, 147.12) * mm});
            skArc(sketch, "E195.0.8.2", {"start": v(17.98, 142.12) * mm, "mid": v(15.48, 144.62) * mm, "end": v(17.98, 147.12) * mm});
            skLineSegment(sketch, "E195.0.8.3", {"start": v(17.98, 144.62) * mm, "end": v(32.98, 144.62) * mm, "construction": true});
            skArc(sketch, "E195.0.8.4", {"start": v(32.98, 147.12) * mm, "mid": v(35.48, 144.62) * mm, "end": v(32.98, 142.12) * mm});
            skLineSegment(sketch, "E195.0.9.0", {"start": v(17.98, 132.12) * mm, "end": v(32.98, 132.12) * mm});
            skLineSegment(sketch, "E195.0.9.1", {"start": v(17.98, 137.12) * mm, "end": v(32.98, 137.12) * mm});
            skArc(sketch, "E195.0.9.2", {"start": v(17.98, 132.12) * mm, "mid": v(15.48, 134.62) * mm, "end": v(17.98, 137.12) * mm});
            skLineSegment(sketch, "E195.0.9.3", {"start": v(17.98, 134.62) * mm, "end": v(32.98, 134.62) * mm, "construction": true});
            skArc(sketch, "E195.0.9.4", {"start": v(32.98, 137.12) * mm, "mid": v(35.48, 134.62) * mm, "end": v(32.98, 132.12) * mm});
            skLineSegment(sketch, "E195.0.10.0", {"start": v(17.98, 122.12) * mm, "end": v(32.98, 122.12) * mm});
            skLineSegment(sketch, "E195.0.10.1", {"start": v(17.98, 127.12) * mm, "end": v(32.98, 127.12) * mm});
            skArc(sketch, "E195.0.10.2", {"start": v(17.98, 122.12) * mm, "mid": v(15.48, 124.62) * mm, "end": v(17.98, 127.12) * mm});
            skLineSegment(sketch, "E195.0.10.3", {"start": v(17.98, 124.62) * mm, "end": v(32.98, 124.62) * mm, "construction": true});
            skArc(sketch, "E195.0.10.4", {"start": v(32.98, 127.12) * mm, "mid": v(35.48, 124.62) * mm, "end": v(32.98, 122.12) * mm});
            skLineSegment(sketch, "E195.0.11.0", {"start": v(17.98, 112.12) * mm, "end": v(32.98, 112.12) * mm});
            skLineSegment(sketch, "E195.0.11.1", {"start": v(17.98, 117.12) * mm, "end": v(32.98, 117.12) * mm});
            skArc(sketch, "E195.0.11.2", {"start": v(17.98, 112.12) * mm, "mid": v(15.48, 114.62) * mm, "end": v(17.98, 117.12) * mm});
            skLineSegment(sketch, "E195.0.11.3", {"start": v(17.98, 114.62) * mm, "end": v(32.98, 114.62) * mm, "construction": true});
            skArc(sketch, "E195.0.11.4", {"start": v(32.98, 117.12) * mm, "mid": v(35.48, 114.62) * mm, "end": v(32.98, 112.12) * mm});
            skLineSegment(sketch, "E195.0.12.0", {"start": v(17.98, 102.12) * mm, "end": v(32.98, 102.12) * mm});
            skLineSegment(sketch, "E195.0.12.1", {"start": v(17.98, 107.12) * mm, "end": v(32.98, 107.12) * mm});
            skArc(sketch, "E195.0.12.2", {"start": v(17.98, 102.12) * mm, "mid": v(15.48, 104.62) * mm, "end": v(17.98, 107.12) * mm});
            skLineSegment(sketch, "E195.0.12.3", {"start": v(17.98, 104.62) * mm, "end": v(32.98, 104.62) * mm, "construction": true});
            skArc(sketch, "E195.0.12.4", {"start": v(32.98, 107.12) * mm, "mid": v(35.48, 104.62) * mm, "end": v(32.98, 102.12) * mm});
            skLineSegment(sketch, "E195.0.13.0", {"start": v(17.98, 92.12) * mm, "end": v(32.98, 92.12) * mm});
            skLineSegment(sketch, "E195.0.13.1", {"start": v(17.98, 97.12) * mm, "end": v(32.98, 97.12) * mm});
            skArc(sketch, "E195.0.13.2", {"start": v(17.98, 92.12) * mm, "mid": v(15.48, 94.62) * mm, "end": v(17.98, 97.12) * mm});
            skLineSegment(sketch, "E195.0.13.3", {"start": v(17.98, 94.62) * mm, "end": v(32.98, 94.62) * mm, "construction": true});
            skArc(sketch, "E195.0.13.4", {"start": v(32.98, 97.12) * mm, "mid": v(35.48, 94.62) * mm, "end": v(32.98, 92.12) * mm});
            skLineSegment(sketch, "E195.0.14.0", {"start": v(17.98, 82.12) * mm, "end": v(32.98, 82.12) * mm});
            skLineSegment(sketch, "E195.0.14.1", {"start": v(17.98, 87.12) * mm, "end": v(32.98, 87.12) * mm});
            skArc(sketch, "E195.0.14.2", {"start": v(17.98, 82.12) * mm, "mid": v(15.48, 84.62) * mm, "end": v(17.98, 87.12) * mm});
            skLineSegment(sketch, "E195.0.14.3", {"start": v(17.98, 84.62) * mm, "end": v(32.98, 84.62) * mm, "construction": true});
            skArc(sketch, "E195.0.14.4", {"start": v(32.98, 87.12) * mm, "mid": v(35.48, 84.62) * mm, "end": v(32.98, 82.12) * mm});
            skLineSegment(sketch, "E195.direction1", {"start": v(17.98, 222.12) * mm, "end": v(21.97, 222.12) * mm, "construction": true});
            skLineSegment(sketch, "E195.direction2", {"start": v(17.98, 222.12) * mm, "end": v(17.98, 212.12) * mm, "construction": true});
            skLineSegment(sketch, "E196.bottom", {"start": v(-72.02, 83.02) * mm, "end": v(4.58, 83.02) * mm, "construction": true});
            skLineSegment(sketch, "E196.top", {"start": v(-72.02, 144.72) * mm, "end": v(4.58, 144.72) * mm, "construction": true});
            skLineSegment(sketch, "E196.left", {"start": v(-72.02, 83.02) * mm, "end": v(-72.02, 144.72) * mm, "construction": true});
            skLineSegment(sketch, "E196.right", {"start": v(4.58, 83.02) * mm, "end": v(4.58, 144.72) * mm, "construction": true});
            skLineSegment(sketch, "E197", {"start": v(-72.02, 113.87) * mm, "end": v(-87.02, 113.87) * mm, "construction": true});
            skLineSegment(sketch, "E198.bottom", {"start": v(-72.02, 156.02) * mm, "end": v(4.58, 156.02) * mm, "construction": true});
            skLineSegment(sketch, "E198.top", {"start": v(-72.02, 217.72) * mm, "end": v(4.58, 217.72) * mm, "construction": true});
            skLineSegment(sketch, "E198.left", {"start": v(-72.02, 156.02) * mm, "end": v(-72.02, 217.72) * mm, "construction": true});
            skLineSegment(sketch, "E198.right", {"start": v(4.58, 156.02) * mm, "end": v(4.58, 217.72) * mm, "construction": true});
            skLineSegment(sketch, "E199", {"start": v(-72.02, 186.87) * mm, "end": v(-87.02, 186.87) * mm, "construction": true});
            skCircle(sketch, "E200", {"center": v(4.58, 83.02) * mm, "radius": 1.6 * mm});
            skCircle(sketch, "E201", {"center": v(4.58, 144.72) * mm, "radius": 1.6 * mm});
            skCircle(sketch, "E202", {"center": v(-72.02, 144.72) * mm, "radius": 1.6 * mm});
            skCircle(sketch, "E203", {"center": v(-72.02, 83.02) * mm, "radius": 1.6 * mm});
            skCircle(sketch, "E204", {"center": v(-72.02, 156.02) * mm, "radius": 1.6 * mm});
            skCircle(sketch, "E205", {"center": v(-72.02, 217.72) * mm, "radius": 1.6 * mm});
            skCircle(sketch, "E206", {"center": v(4.58, 217.72) * mm, "radius": 1.6 * mm});
            skCircle(sketch, "E207", {"center": v(4.58, 156.02) * mm, "radius": 1.6 * mm});
            skSolve(sketch);
        }
        {
            var Q0;
            Q0=qSketchRegion(id+"F33",true);
            extrude(context, id + "F34", {"entities" : qUnion([Q0]), "operationType" : NewBodyOperationType.REMOVE, "oppositeDirection" : true, "depth" : 25 * mm});
        }
        {
            var Q0;
            {var subQ0=makeQuery(id+"F23.opExtrude","CAP_FACE",FACE,{"disambiguationData":[OSD([sQuery(id+"F22.wireOp",EDGE,"E125.bottom"),sQuery(id+"F22.wireOp",EDGE,"E125.top"),sQuery(id+"F22.wireOp",EDGE,"E125.left"),sQuery(id+"F22.wireOp",EDGE,"E125.right"),sQuery(id+"F22.wireOp",EDGE,"E126"),sQuery(id+"F22.wireOp",EDGE,"E127"),sQuery(id+"F22.wireOp",EDGE,"E128"),sQuery(id+"F22.wireOp",EDGE,"E129")])],"isStart":true});Q0=makeQuery(id+"F24.boolean.opBoolean","MERGE",FACE,{"derivedFrom":[subQ0,makeQuery(id+"F24.opPattern","COPY",FACE,{"derivedFrom":subQ0,"instanceName":"1"})]});}
            var sketch = newSketch(context, id + "F35", { "sketchPlane" : qUnion([Q0])});
            skLineSegment(sketch, "E208", {"start": v(-63.42, -169.92) * mm, "end": v(51.58, -169.92) * mm, "construction": true});
            skLineSegment(sketch, "E209", {"start": v(-58.42, -169.92) * mm, "end": v(-58.42, -154.92) * mm, "construction": true});
            skLineSegment(sketch, "E210", {"start": v(-58.42, -154.92) * mm, "end": v(-58.42, -121.47) * mm, "construction": true});
            skLineSegment(sketch, "E211", {"start": v(46.58, -169.92) * mm, "end": v(46.58, -154.92) * mm, "construction": true});
            skLineSegment(sketch, "E212", {"start": v(46.58, -154.92) * mm, "end": v(46.58, -124.42) * mm, "construction": true});
            skCircle(sketch, "E213", {"center": v(-58.42, -169.92) * mm, "radius": 2.55 * mm});
            skLineSegment(sketch, "E214", {"start": v(-58.42, -74.92) * mm, "end": v(-58.42, -64.92) * mm, "construction": true});
            skPoint(sketch, "E214.endSnap0", {"position": v(-58.42, -69.1) * mm});
            skCircle(sketch, "E215", {"center": v(-58.42, -64.92) * mm, "radius": 2.55 * mm});
            skLineSegment(sketch, "E216", {"start": v(-58.42, -121.47) * mm, "end": v(-58.42, -108.37) * mm, "construction": true});
            skLineSegment(sketch, "E217", {"start": v(-58.42, -108.37) * mm, "end": v(-58.42, -74.92) * mm, "construction": true});
            skArc(sketch, "E218.0.startCap", {"start": v(-53.42, -154.92) * mm, "mid": v(-58.42, -159.92) * mm, "end": v(-63.42, -154.92) * mm});
            skArc(sketch, "E218.0.endCap", {"start": v(-63.42, -121.47) * mm, "mid": v(-58.42, -116.47) * mm, "end": v(-53.42, -121.47) * mm});
            skLineSegment(sketch, "E218.0.left", {"start": v(-63.42, -154.92) * mm, "end": v(-63.42, -121.47) * mm});
            skLineSegment(sketch, "E218.0.right", {"start": v(-53.42, -154.92) * mm, "end": v(-53.42, -121.47) * mm});
            skArc(sketch, "E218.1.startCap", {"start": v(-53.42, -108.37) * mm, "mid": v(-58.42, -113.37) * mm, "end": v(-63.42, -108.37) * mm});
            skArc(sketch, "E218.1.endCap", {"start": v(-63.42, -74.92) * mm, "mid": v(-58.42, -69.92) * mm, "end": v(-53.42, -74.92) * mm});
            skLineSegment(sketch, "E218.1.left", {"start": v(-63.42, -108.37) * mm, "end": v(-63.42, -74.92) * mm});
            skLineSegment(sketch, "E218.1.right", {"start": v(-53.42, -108.37) * mm, "end": v(-53.42, -74.92) * mm});
            skLineSegment(sketch, "E219", {"start": v(46.58, -124.42) * mm, "end": v(46.58, -110.42) * mm, "construction": true});
            skLineSegment(sketch, "E220", {"start": v(46.58, -110.42) * mm, "end": v(46.58, -79.92) * mm, "construction": true});
            skLineSegment(sketch, "E221", {"start": v(46.58, -79.92) * mm, "end": v(46.58, -64.92) * mm, "construction": true});
            skArc(sketch, "E222.5.startCap", {"start": v(51.58, -154.92) * mm, "mid": v(46.58, -159.92) * mm, "end": v(41.58, -154.92) * mm});
            skArc(sketch, "E222.5.endCap", {"start": v(41.58, -124.42) * mm, "mid": v(46.58, -119.42) * mm, "end": v(51.58, -124.42) * mm});
            skLineSegment(sketch, "E222.5.left", {"start": v(41.58, -154.92) * mm, "end": v(41.58, -124.42) * mm});
            skLineSegment(sketch, "E222.5.right", {"start": v(51.58, -154.92) * mm, "end": v(51.58, -124.42) * mm});
            skArc(sketch, "E222.6.startCap", {"start": v(51.58, -110.42) * mm, "mid": v(46.58, -115.42) * mm, "end": v(41.58, -110.42) * mm});
            skArc(sketch, "E222.6.endCap", {"start": v(41.58, -79.92) * mm, "mid": v(46.58, -74.92) * mm, "end": v(51.58, -79.92) * mm});
            skLineSegment(sketch, "E222.6.left", {"start": v(41.58, -110.42) * mm, "end": v(41.58, -79.92) * mm});
            skLineSegment(sketch, "E222.6.right", {"start": v(51.58, -110.42) * mm, "end": v(51.58, -79.92) * mm});
            skCircle(sketch, "E223", {"center": v(46.58, -169.92) * mm, "radius": 2.55 * mm});
            skCircle(sketch, "E224", {"center": v(46.58, -64.92) * mm, "radius": 2.55 * mm});
            skLineSegment(sketch, "E225", {"start": v(-63.42, -169.92) * mm, "end": v(-63.42, -209.42) * mm, "construction": true});
            skLineSegment(sketch, "E226", {"start": v(-58.42, -64.92) * mm, "end": v(-58.42, -25.42) * mm, "construction": true});
            skLineSegment(sketch, "E227", {"start": v(-45.3, -169.92) * mm, "end": v(-45.3, -143.66) * mm, "construction": true});
            skLineSegment(sketch, "E228", {"start": v(-45.3, -143.66) * mm, "end": v(-45.3, -130.56) * mm, "construction": true});
            skLineSegment(sketch, "E229", {"start": v(-45.3, -130.56) * mm, "end": v(-45.3, -104.3) * mm, "construction": true});
            skLineSegment(sketch, "E230", {"start": v(-45.3, -104.3) * mm, "end": v(-45.3, -91.2) * mm, "construction": true});
            skLineSegment(sketch, "E231", {"start": v(-45.3, -64.92) * mm, "end": v(-45.3, -91.2) * mm, "construction": true});
            skLineSegment(sketch, "E232", {"start": v(-58.42, -64.92) * mm, "end": v(-45.3, -64.92) * mm, "construction": true});
            skArc(sketch, "E233.0.startCap", {"start": v(-40.3, -169.92) * mm, "mid": v(-45.3, -174.92) * mm, "end": v(-50.3, -169.92) * mm});
            skArc(sketch, "E233.0.endCap", {"start": v(-50.3, -143.66) * mm, "mid": v(-45.3, -138.66) * mm, "end": v(-40.3, -143.66) * mm});
            skLineSegment(sketch, "E233.0.left", {"start": v(-50.3, -169.92) * mm, "end": v(-50.3, -143.66) * mm});
            skLineSegment(sketch, "E233.0.right", {"start": v(-40.3, -169.92) * mm, "end": v(-40.3, -143.66) * mm});
            skArc(sketch, "E233.1.startCap", {"start": v(-40.3, -130.56) * mm, "mid": v(-45.3, -135.56) * mm, "end": v(-50.3, -130.56) * mm});
            skArc(sketch, "E233.1.endCap", {"start": v(-50.3, -104.3) * mm, "mid": v(-45.3, -99.3) * mm, "end": v(-40.3, -104.3) * mm});
            skLineSegment(sketch, "E233.1.left", {"start": v(-50.3, -130.56) * mm, "end": v(-50.3, -104.3) * mm});
            skLineSegment(sketch, "E233.1.right", {"start": v(-40.3, -130.56) * mm, "end": v(-40.3, -104.3) * mm});
            skArc(sketch, "E233.2.startCap", {"start": v(-50.3, -64.92) * mm, "mid": v(-45.3, -59.92) * mm, "end": v(-40.3, -64.92) * mm});
            skArc(sketch, "E233.2.endCap", {"start": v(-40.3, -91.2) * mm, "mid": v(-45.3, -96.2) * mm, "end": v(-50.3, -91.2) * mm});
            skLineSegment(sketch, "E233.2.left", {"start": v(-40.3, -64.92) * mm, "end": v(-40.3, -91.2) * mm});
            skLineSegment(sketch, "E233.2.right", {"start": v(-50.3, -64.92) * mm, "end": v(-50.3, -91.2) * mm});
            skLineSegment(sketch, "E234.1.0.0", {"start": v(-32.17, -104.3) * mm, "end": v(-32.17, -91.2) * mm, "construction": true});
            skArc(sketch, "E234.1.0.1", {"start": v(-27.17, -130.56) * mm, "mid": v(-32.17, -135.56) * mm, "end": v(-37.17, -130.56) * mm});
            skLineSegment(sketch, "E234.1.0.2", {"start": v(-27.17, -130.56) * mm, "end": v(-27.17, -104.3) * mm});
            skArc(sketch, "E234.1.0.3", {"start": v(-37.17, -143.66) * mm, "mid": v(-32.17, -138.66) * mm, "end": v(-27.17, -143.66) * mm});
            skLineSegment(sketch, "E234.1.0.4", {"start": v(-27.17, -169.92) * mm, "end": v(-27.17, -143.66) * mm});
            skPoint(sketch, "E234.1.0.5", {"position": v(-45.3, -69.1) * mm});
            skArc(sketch, "E234.1.0.6", {"start": v(-27.17, -169.92) * mm, "mid": v(-32.17, -174.92) * mm, "end": v(-37.17, -169.92) * mm});
            skLineSegment(sketch, "E234.1.0.7", {"start": v(-32.17, -169.92) * mm, "end": v(-32.17, -143.66) * mm, "construction": true});
            skLineSegment(sketch, "E234.1.0.8", {"start": v(-32.17, -143.66) * mm, "end": v(-32.17, -130.56) * mm, "construction": true});
            skLineSegment(sketch, "E234.1.0.9", {"start": v(-37.17, -169.92) * mm, "end": v(-37.17, -143.66) * mm});
            skLineSegment(sketch, "E234.1.0.10", {"start": v(-32.17, -130.56) * mm, "end": v(-32.17, -104.3) * mm, "construction": true});
            skArc(sketch, "E234.1.0.11", {"start": v(-37.17, -104.3) * mm, "mid": v(-32.17, -99.3) * mm, "end": v(-27.17, -104.3) * mm});
            skLineSegment(sketch, "E234.1.0.12", {"start": v(-37.17, -64.92) * mm, "end": v(-37.17, -91.2) * mm});
            skLineSegment(sketch, "E234.1.0.13", {"start": v(-37.17, -130.56) * mm, "end": v(-37.17, -104.3) * mm});
            skArc(sketch, "E234.1.0.14", {"start": v(-27.17, -91.2) * mm, "mid": v(-32.17, -96.2) * mm, "end": v(-37.17, -91.2) * mm});
            skLineSegment(sketch, "E234.1.0.15", {"start": v(-32.17, -64.92) * mm, "end": v(-32.17, -91.2) * mm, "construction": true});
            skLineSegment(sketch, "E234.1.0.16", {"start": v(-27.17, -64.92) * mm, "end": v(-27.17, -91.2) * mm});
            skArc(sketch, "E234.1.0.17", {"start": v(-37.17, -64.92) * mm, "mid": v(-32.17, -59.92) * mm, "end": v(-27.17, -64.92) * mm});
            skLineSegment(sketch, "E234.2.0.0", {"start": v(-19.05, -104.3) * mm, "end": v(-19.05, -91.2) * mm, "construction": true});
            skArc(sketch, "E234.2.0.1", {"start": v(-14.05, -130.56) * mm, "mid": v(-19.05, -135.56) * mm, "end": v(-24.05, -130.56) * mm});
            skLineSegment(sketch, "E234.2.0.2", {"start": v(-14.05, -130.56) * mm, "end": v(-14.05, -104.3) * mm});
            skArc(sketch, "E234.2.0.3", {"start": v(-24.05, -143.66) * mm, "mid": v(-19.05, -138.66) * mm, "end": v(-14.05, -143.66) * mm});
            skLineSegment(sketch, "E234.2.0.4", {"start": v(-14.05, -169.92) * mm, "end": v(-14.05, -143.66) * mm});
            skPoint(sketch, "E234.2.0.5", {"position": v(-32.17, -69.1) * mm});
            skArc(sketch, "E234.2.0.6", {"start": v(-14.05, -169.92) * mm, "mid": v(-19.05, -174.92) * mm, "end": v(-24.05, -169.92) * mm});
            skLineSegment(sketch, "E234.2.0.7", {"start": v(-19.05, -169.92) * mm, "end": v(-19.05, -143.66) * mm, "construction": true});
            skLineSegment(sketch, "E234.2.0.8", {"start": v(-19.05, -143.66) * mm, "end": v(-19.05, -130.56) * mm, "construction": true});
            skLineSegment(sketch, "E234.2.0.9", {"start": v(-24.05, -169.92) * mm, "end": v(-24.05, -143.66) * mm});
            skLineSegment(sketch, "E234.2.0.10", {"start": v(-19.05, -130.56) * mm, "end": v(-19.05, -104.3) * mm, "construction": true});
            skArc(sketch, "E234.2.0.11", {"start": v(-24.05, -104.3) * mm, "mid": v(-19.05, -99.3) * mm, "end": v(-14.05, -104.3) * mm});
            skLineSegment(sketch, "E234.2.0.12", {"start": v(-24.05, -64.92) * mm, "end": v(-24.05, -91.2) * mm});
            skLineSegment(sketch, "E234.2.0.13", {"start": v(-24.05, -130.56) * mm, "end": v(-24.05, -104.3) * mm});
            skArc(sketch, "E234.2.0.14", {"start": v(-14.05, -91.2) * mm, "mid": v(-19.05, -96.2) * mm, "end": v(-24.05, -91.2) * mm});
            skLineSegment(sketch, "E234.2.0.15", {"start": v(-19.05, -64.92) * mm, "end": v(-19.05, -91.2) * mm, "construction": true});
            skLineSegment(sketch, "E234.2.0.16", {"start": v(-14.05, -64.92) * mm, "end": v(-14.05, -91.2) * mm});
            skArc(sketch, "E234.2.0.17", {"start": v(-24.05, -64.92) * mm, "mid": v(-19.05, -59.92) * mm, "end": v(-14.05, -64.92) * mm});
            skLineSegment(sketch, "E234.3.0.0", {"start": v(-5.92, -104.3) * mm, "end": v(-5.92, -91.2) * mm, "construction": true});
            skArc(sketch, "E234.3.0.1", {"start": v(-0.92, -130.56) * mm, "mid": v(-5.92, -135.56) * mm, "end": v(-10.92, -130.56) * mm});
            skLineSegment(sketch, "E234.3.0.2", {"start": v(-0.92, -130.56) * mm, "end": v(-0.92, -104.3) * mm});
            skArc(sketch, "E234.3.0.3", {"start": v(-10.92, -143.66) * mm, "mid": v(-5.92, -138.66) * mm, "end": v(-0.92, -143.66) * mm});
            skLineSegment(sketch, "E234.3.0.4", {"start": v(-0.92, -169.92) * mm, "end": v(-0.92, -143.66) * mm});
            skPoint(sketch, "E234.3.0.5", {"position": v(-19.05, -69.1) * mm});
            skArc(sketch, "E234.3.0.6", {"start": v(-0.92, -169.92) * mm, "mid": v(-5.92, -174.92) * mm, "end": v(-10.92, -169.92) * mm});
            skLineSegment(sketch, "E234.3.0.7", {"start": v(-5.92, -169.92) * mm, "end": v(-5.92, -143.66) * mm, "construction": true});
            skLineSegment(sketch, "E234.3.0.8", {"start": v(-5.92, -143.66) * mm, "end": v(-5.92, -130.56) * mm, "construction": true});
            skLineSegment(sketch, "E234.3.0.9", {"start": v(-10.92, -169.92) * mm, "end": v(-10.92, -143.66) * mm});
            skLineSegment(sketch, "E234.3.0.10", {"start": v(-5.92, -130.56) * mm, "end": v(-5.92, -104.3) * mm, "construction": true});
            skArc(sketch, "E234.3.0.11", {"start": v(-10.92, -104.3) * mm, "mid": v(-5.92, -99.3) * mm, "end": v(-0.92, -104.3) * mm});
            skLineSegment(sketch, "E234.3.0.12", {"start": v(-10.92, -64.92) * mm, "end": v(-10.92, -91.2) * mm});
            skLineSegment(sketch, "E234.3.0.13", {"start": v(-10.92, -130.56) * mm, "end": v(-10.92, -104.3) * mm});
            skArc(sketch, "E234.3.0.14", {"start": v(-0.92, -91.2) * mm, "mid": v(-5.92, -96.2) * mm, "end": v(-10.92, -91.2) * mm});
            skLineSegment(sketch, "E234.3.0.15", {"start": v(-5.92, -64.92) * mm, "end": v(-5.92, -91.2) * mm, "construction": true});
            skLineSegment(sketch, "E234.3.0.16", {"start": v(-0.92, -64.92) * mm, "end": v(-0.92, -91.2) * mm});
            skArc(sketch, "E234.3.0.17", {"start": v(-10.92, -64.92) * mm, "mid": v(-5.92, -59.92) * mm, "end": v(-0.92, -64.92) * mm});
            skLineSegment(sketch, "E234.4.0.0", {"start": v(7.2, -104.3) * mm, "end": v(7.2, -91.2) * mm, "construction": true});
            skArc(sketch, "E234.4.0.1", {"start": v(12.2, -130.56) * mm, "mid": v(7.2, -135.56) * mm, "end": v(2.2, -130.56) * mm});
            skLineSegment(sketch, "E234.4.0.2", {"start": v(12.2, -130.56) * mm, "end": v(12.2, -104.3) * mm});
            skArc(sketch, "E234.4.0.3", {"start": v(2.2, -143.66) * mm, "mid": v(7.2, -138.66) * mm, "end": v(12.2, -143.66) * mm});
            skLineSegment(sketch, "E234.4.0.4", {"start": v(12.2, -169.92) * mm, "end": v(12.2, -143.66) * mm});
            skPoint(sketch, "E234.4.0.5", {"position": v(-5.92, -69.1) * mm});
            skArc(sketch, "E234.4.0.6", {"start": v(12.2, -169.92) * mm, "mid": v(7.2, -174.92) * mm, "end": v(2.2, -169.92) * mm});
            skLineSegment(sketch, "E234.4.0.7", {"start": v(7.2, -169.92) * mm, "end": v(7.2, -143.66) * mm, "construction": true});
            skLineSegment(sketch, "E234.4.0.8", {"start": v(7.2, -143.66) * mm, "end": v(7.2, -130.56) * mm, "construction": true});
            skLineSegment(sketch, "E234.4.0.9", {"start": v(2.2, -169.92) * mm, "end": v(2.2, -143.66) * mm});
            skLineSegment(sketch, "E234.4.0.10", {"start": v(7.2, -130.56) * mm, "end": v(7.2, -104.3) * mm, "construction": true});
            skArc(sketch, "E234.4.0.11", {"start": v(2.2, -104.3) * mm, "mid": v(7.2, -99.3) * mm, "end": v(12.2, -104.3) * mm});
            skLineSegment(sketch, "E234.4.0.12", {"start": v(2.2, -64.92) * mm, "end": v(2.2, -91.2) * mm});
            skLineSegment(sketch, "E234.4.0.13", {"start": v(2.2, -130.56) * mm, "end": v(2.2, -104.3) * mm});
            skArc(sketch, "E234.4.0.14", {"start": v(12.2, -91.2) * mm, "mid": v(7.2, -96.2) * mm, "end": v(2.2, -91.2) * mm});
            skLineSegment(sketch, "E234.4.0.15", {"start": v(7.2, -64.92) * mm, "end": v(7.2, -91.2) * mm, "construction": true});
            skLineSegment(sketch, "E234.4.0.16", {"start": v(12.2, -64.92) * mm, "end": v(12.2, -91.2) * mm});
            skArc(sketch, "E234.4.0.17", {"start": v(2.2, -64.92) * mm, "mid": v(7.2, -59.92) * mm, "end": v(12.2, -64.92) * mm});
            skLineSegment(sketch, "E234.5.0.0", {"start": v(20.33, -104.3) * mm, "end": v(20.33, -91.2) * mm, "construction": true});
            skArc(sketch, "E234.5.0.1", {"start": v(25.33, -130.56) * mm, "mid": v(20.33, -135.56) * mm, "end": v(15.33, -130.56) * mm});
            skLineSegment(sketch, "E234.5.0.2", {"start": v(25.33, -130.56) * mm, "end": v(25.33, -104.3) * mm});
            skArc(sketch, "E234.5.0.3", {"start": v(15.33, -143.66) * mm, "mid": v(20.33, -138.66) * mm, "end": v(25.33, -143.66) * mm});
            skLineSegment(sketch, "E234.5.0.4", {"start": v(25.33, -169.92) * mm, "end": v(25.33, -143.66) * mm});
            skPoint(sketch, "E234.5.0.5", {"position": v(7.2, -69.1) * mm});
            skArc(sketch, "E234.5.0.6", {"start": v(25.33, -169.92) * mm, "mid": v(20.33, -174.92) * mm, "end": v(15.33, -169.92) * mm});
            skLineSegment(sketch, "E234.5.0.7", {"start": v(20.33, -169.92) * mm, "end": v(20.33, -143.66) * mm, "construction": true});
            skLineSegment(sketch, "E234.5.0.8", {"start": v(20.33, -143.66) * mm, "end": v(20.33, -130.56) * mm, "construction": true});
            skLineSegment(sketch, "E234.5.0.9", {"start": v(15.33, -169.92) * mm, "end": v(15.33, -143.66) * mm});
            skLineSegment(sketch, "E234.5.0.10", {"start": v(20.33, -130.56) * mm, "end": v(20.33, -104.3) * mm, "construction": true});
            skArc(sketch, "E234.5.0.11", {"start": v(15.33, -104.3) * mm, "mid": v(20.33, -99.3) * mm, "end": v(25.33, -104.3) * mm});
            skLineSegment(sketch, "E234.5.0.12", {"start": v(15.33, -64.92) * mm, "end": v(15.33, -91.2) * mm});
            skLineSegment(sketch, "E234.5.0.13", {"start": v(15.33, -130.56) * mm, "end": v(15.33, -104.3) * mm});
            skArc(sketch, "E234.5.0.14", {"start": v(25.33, -91.2) * mm, "mid": v(20.33, -96.2) * mm, "end": v(15.33, -91.2) * mm});
            skLineSegment(sketch, "E234.5.0.15", {"start": v(20.33, -64.92) * mm, "end": v(20.33, -91.2) * mm, "construction": true});
            skLineSegment(sketch, "E234.5.0.16", {"start": v(25.33, -64.92) * mm, "end": v(25.33, -91.2) * mm});
            skArc(sketch, "E234.5.0.17", {"start": v(15.33, -64.92) * mm, "mid": v(20.33, -59.92) * mm, "end": v(25.33, -64.92) * mm});
            skLineSegment(sketch, "E234.6.0.0", {"start": v(33.45, -104.3) * mm, "end": v(33.45, -91.2) * mm, "construction": true});
            skArc(sketch, "E234.6.0.1", {"start": v(38.45, -130.56) * mm, "mid": v(33.45, -135.56) * mm, "end": v(28.45, -130.56) * mm});
            skLineSegment(sketch, "E234.6.0.2", {"start": v(38.45, -130.56) * mm, "end": v(38.45, -104.3) * mm});
            skArc(sketch, "E234.6.0.3", {"start": v(28.45, -143.66) * mm, "mid": v(33.45, -138.66) * mm, "end": v(38.45, -143.66) * mm});
            skLineSegment(sketch, "E234.6.0.4", {"start": v(38.45, -169.92) * mm, "end": v(38.45, -143.66) * mm});
            skPoint(sketch, "E234.6.0.5", {"position": v(20.33, -69.1) * mm});
            skArc(sketch, "E234.6.0.6", {"start": v(38.45, -169.92) * mm, "mid": v(33.45, -174.92) * mm, "end": v(28.45, -169.92) * mm});
            skLineSegment(sketch, "E234.6.0.7", {"start": v(33.45, -169.92) * mm, "end": v(33.45, -143.66) * mm, "construction": true});
            skLineSegment(sketch, "E234.6.0.8", {"start": v(33.45, -143.66) * mm, "end": v(33.45, -130.56) * mm, "construction": true});
            skLineSegment(sketch, "E234.6.0.9", {"start": v(28.45, -169.92) * mm, "end": v(28.45, -143.66) * mm});
            skLineSegment(sketch, "E234.6.0.10", {"start": v(33.45, -130.56) * mm, "end": v(33.45, -104.3) * mm, "construction": true});
            skArc(sketch, "E234.6.0.11", {"start": v(28.45, -104.3) * mm, "mid": v(33.45, -99.3) * mm, "end": v(38.45, -104.3) * mm});
            skLineSegment(sketch, "E234.6.0.12", {"start": v(28.45, -64.92) * mm, "end": v(28.45, -91.2) * mm});
            skLineSegment(sketch, "E234.6.0.13", {"start": v(28.45, -130.56) * mm, "end": v(28.45, -104.3) * mm});
            skArc(sketch, "E234.6.0.14", {"start": v(38.45, -91.2) * mm, "mid": v(33.45, -96.2) * mm, "end": v(28.45, -91.2) * mm});
            skLineSegment(sketch, "E234.6.0.15", {"start": v(33.45, -64.92) * mm, "end": v(33.45, -91.2) * mm, "construction": true});
            skLineSegment(sketch, "E234.6.0.16", {"start": v(38.45, -64.92) * mm, "end": v(38.45, -91.2) * mm});
            skArc(sketch, "E234.6.0.17", {"start": v(28.45, -64.92) * mm, "mid": v(33.45, -59.92) * mm, "end": v(38.45, -64.92) * mm});
            skLineSegment(sketch, "E234.direction1", {"start": v(-50.3, -169.92) * mm, "end": v(-37.17, -169.92) * mm, "construction": true});
            skLineSegment(sketch, "E235", {"start": v(61.08, -42.92) * mm, "end": v(39.58, -42.92) * mm, "construction": true});
            skCircle(sketch, "E236", {"center": v(39.58, -42.92) * mm, "radius": 2 * mm});
            skLineSegment(sketch, "E237", {"start": v(61.08, -191.92) * mm, "end": v(39.58, -191.92) * mm, "construction": true});
            skCircle(sketch, "E238", {"center": v(39.58, -191.92) * mm, "radius": 2 * mm});
            skLineSegment(sketch, "E239", {"start": v(-72.92, -42.92) * mm, "end": v(-51.42, -42.92) * mm, "construction": true});
            skCircle(sketch, "E240", {"center": v(-51.42, -42.92) * mm, "radius": 2 * mm});
            skLineSegment(sketch, "E241", {"start": v(-72.92, -191.92) * mm, "end": v(-51.42, -191.92) * mm, "construction": true});
            skCircle(sketch, "E242", {"center": v(-51.42, -191.92) * mm, "radius": 2 * mm});
            skSolve(sketch);
        }
        {
            var Q0;
            Q0=qSketchRegion(id+"F35",true);
            extrude(context, id + "F36", {"entities" : qUnion([Q0]), "operationType" : NewBodyOperationType.REMOVE, "oppositeDirection" : true, "depth" : 25 * mm});
        }
        {
            var Q0;
            Q0=qCreatedBy(id+"F25.planeOp",FACE);
            var sketch = newSketch(context, id + "F37", { "sketchPlane" : qUnion([Q0])});
            skLineSegment(sketch, "E243", {"start": v(-112.23, -42.59) * mm, "end": v(-112.23, -95.59) * mm, "construction": true});
            skCircle(sketch, "E244", {"center": v(-112.23, -95.59) * mm, "radius": 1.6 * mm});
            skCircle(sketch, "E245", {"center": v(-112.23, -42.59) * mm, "radius": 1.6 * mm});
            skLineSegment(sketch, "E246.bottom", {"start": v(-100.23, -37.59) * mm, "end": v(-124.23, -37.59) * mm});
            skLineSegment(sketch, "E246.top", {"start": v(-100.23, -100.59) * mm, "end": v(-124.23, -100.59) * mm});
            skLineSegment(sketch, "E246.left", {"start": v(-100.23, -37.59) * mm, "end": v(-100.23, -100.59) * mm});
            skLineSegment(sketch, "E246.right", {"start": v(-124.23, -37.59) * mm, "end": v(-124.23, -100.59) * mm});
            skLineSegment(sketch, "E247", {"start": v(-112.23, -95.59) * mm, "end": v(-112.23, -100.59) * mm, "construction": true});
            skLineSegment(sketch, "E248", {"start": v(-112.23, -42.59) * mm, "end": v(-112.23, -37.59) * mm, "construction": true});
            skLineSegment(sketch, "E249", {"start": v(-102.23, -100.59) * mm, "end": v(-102.23, -37.59) * mm, "construction": true});
            skLineSegment(sketch, "E250", {"start": v(-100.23, -50.59) * mm, "end": v(-103.33, -50.59) * mm});
            skLineSegment(sketch, "E251", {"start": v(-103.33, -50.59) * mm, "end": v(-103.33, -90.59) * mm});
            skLineSegment(sketch, "E252", {"start": v(-103.33, -90.59) * mm, "end": v(-100.23, -90.59) * mm});
            skLineSegment(sketch, "E253", {"start": v(-119.23, -37.59) * mm, "end": v(-124.23, -42.59) * mm});
            skLineSegment(sketch, "E254", {"start": v(-119.23, -100.59) * mm, "end": v(-124.23, -95.59) * mm});
            skLineSegment(sketch, "E255", {"start": v(-124.23, -50.59) * mm, "end": v(-118.73, -50.59) * mm, "construction": true});
            skLineSegment(sketch, "E256", {"start": v(-118.73, -50.59) * mm, "end": v(-108.73, -50.59) * mm, "construction": true});
            skArc(sketch, "E257.0.startCap", {"start": v(-118.73, -52.59) * mm, "mid": v(-120.73, -50.59) * mm, "end": v(-118.73, -48.59) * mm});
            skArc(sketch, "E257.0.endCap", {"start": v(-108.73, -48.59) * mm, "mid": v(-106.73, -50.59) * mm, "end": v(-108.73, -52.59) * mm});
            skLineSegment(sketch, "E257.0.left", {"start": v(-118.73, -48.59) * mm, "end": v(-108.73, -48.59) * mm});
            skLineSegment(sketch, "E257.0.right", {"start": v(-118.73, -52.59) * mm, "end": v(-108.73, -52.59) * mm});
            skLineSegment(sketch, "E258.0.1.0", {"start": v(-118.73, -58.09) * mm, "end": v(-108.73, -58.09) * mm});
            skArc(sketch, "E258.0.1.1", {"start": v(-108.73, -58.09) * mm, "mid": v(-106.73, -60.09) * mm, "end": v(-108.73, -62.09) * mm});
            skLineSegment(sketch, "E258.0.1.2", {"start": v(-118.73, -62.09) * mm, "end": v(-108.73, -62.09) * mm});
            skArc(sketch, "E258.0.1.3", {"start": v(-118.73, -62.09) * mm, "mid": v(-120.73, -60.09) * mm, "end": v(-118.73, -58.09) * mm});
            skLineSegment(sketch, "E258.0.2.0", {"start": v(-118.73, -67.59) * mm, "end": v(-108.73, -67.59) * mm});
            skArc(sketch, "E258.0.2.1", {"start": v(-108.73, -67.59) * mm, "mid": v(-106.73, -69.59) * mm, "end": v(-108.73, -71.59) * mm});
            skLineSegment(sketch, "E258.0.2.2", {"start": v(-118.73, -71.59) * mm, "end": v(-108.73, -71.59) * mm});
            skArc(sketch, "E258.0.2.3", {"start": v(-118.73, -71.59) * mm, "mid": v(-120.73, -69.59) * mm, "end": v(-118.73, -67.59) * mm});
            skLineSegment(sketch, "E258.0.3.0", {"start": v(-118.73, -77.09) * mm, "end": v(-108.73, -77.09) * mm});
            skArc(sketch, "E258.0.3.1", {"start": v(-108.73, -77.09) * mm, "mid": v(-106.73, -79.09) * mm, "end": v(-108.73, -81.09) * mm});
            skLineSegment(sketch, "E258.0.3.2", {"start": v(-118.73, -81.09) * mm, "end": v(-108.73, -81.09) * mm});
            skArc(sketch, "E258.0.3.3", {"start": v(-118.73, -81.09) * mm, "mid": v(-120.73, -79.09) * mm, "end": v(-118.73, -77.09) * mm});
            skLineSegment(sketch, "E258.0.4.0", {"start": v(-118.73, -86.59) * mm, "end": v(-108.73, -86.59) * mm});
            skArc(sketch, "E258.0.4.1", {"start": v(-108.73, -86.59) * mm, "mid": v(-106.73, -88.59) * mm, "end": v(-108.73, -90.59) * mm});
            skLineSegment(sketch, "E258.0.4.2", {"start": v(-118.73, -90.59) * mm, "end": v(-108.73, -90.59) * mm});
            skArc(sketch, "E258.0.4.3", {"start": v(-118.73, -90.59) * mm, "mid": v(-120.73, -88.59) * mm, "end": v(-118.73, -86.59) * mm});
            skLineSegment(sketch, "E258.direction1", {"start": v(-118.73, -48.59) * mm, "end": v(-93.73, -48.59) * mm, "construction": true});
            skLineSegment(sketch, "E258.direction2", {"start": v(-118.73, -48.59) * mm, "end": v(-118.73, -58.09) * mm, "construction": true});
            skLineSegment(sketch, "E259", {"start": v(-101.23, -90.59) * mm, "end": v(-100.23, -91.59) * mm});
            skLineSegment(sketch, "E260", {"start": v(-101.23, -50.59) * mm, "end": v(-100.23, -49.59) * mm});
            skSolve(sketch);
        }
        {
            var Q0;
            Q0=makeQuery(id+"F37.imprint","IMPRINT",FACE,{"disambiguationData":[TD([[makeQuery(id+"F37.imprint","IMPRINT",EDGE,{"derivedFrom":sQuery(id+"F37.wireOp",EDGE,"E244")}),-1.0]])]});
            extrude(context, id + "F38", {"entities" : qUnion([Q0]), "depth" : 3 * mm});
        }
        {
            var Q0;
            Q0=makeQuery(id+"F10.boolean.opBoolean","COPY",EDGE,{"derivedFrom":makeQuery(id+"F10.opExtrude","SWEPT_EDGE",EDGE,{"disambiguationData":[OSD([sQuery(id+"F9.wireOp",EDGE,"E45.top"),sQuery(id+"F9.wireOp",EDGE,"E45.left")])]})});
            var Q1;
            Q1=makeQuery(id+"F10.boolean.opBoolean","COPY",EDGE,{"derivedFrom":makeQuery(id+"F10.opExtrude","SWEPT_EDGE",EDGE,{"disambiguationData":[OSD([sQuery(id+"F9.wireOp",EDGE,"E43.top"),sQuery(id+"F9.wireOp",EDGE,"E43.left")])]})});
            var Q2;
            Q2=makeQuery(id+"F10.boolean.opBoolean","COPY",EDGE,{"derivedFrom":makeQuery(id+"F10.opExtrude","SWEPT_EDGE",EDGE,{"disambiguationData":[OSD([sQuery(id+"F9.wireOp",EDGE,"E43.bottom"),sQuery(id+"F9.wireOp",EDGE,"E43.left")])]})});
            var Q3;
            Q3=makeQuery(id+"F10.boolean.opBoolean","COPY",EDGE,{"derivedFrom":makeQuery(id+"F10.opExtrude","SWEPT_EDGE",EDGE,{"disambiguationData":[OSD([sQuery(id+"F9.wireOp",EDGE,"E45.bottom"),sQuery(id+"F9.wireOp",EDGE,"E45.left")])]})});
            chamfer(context, id + "F39", {"entities" : qUnion([Q0, Q1, Q2, Q3]), "width" : .5 * mm, "tangentPropagation" : true});
        }
    });
